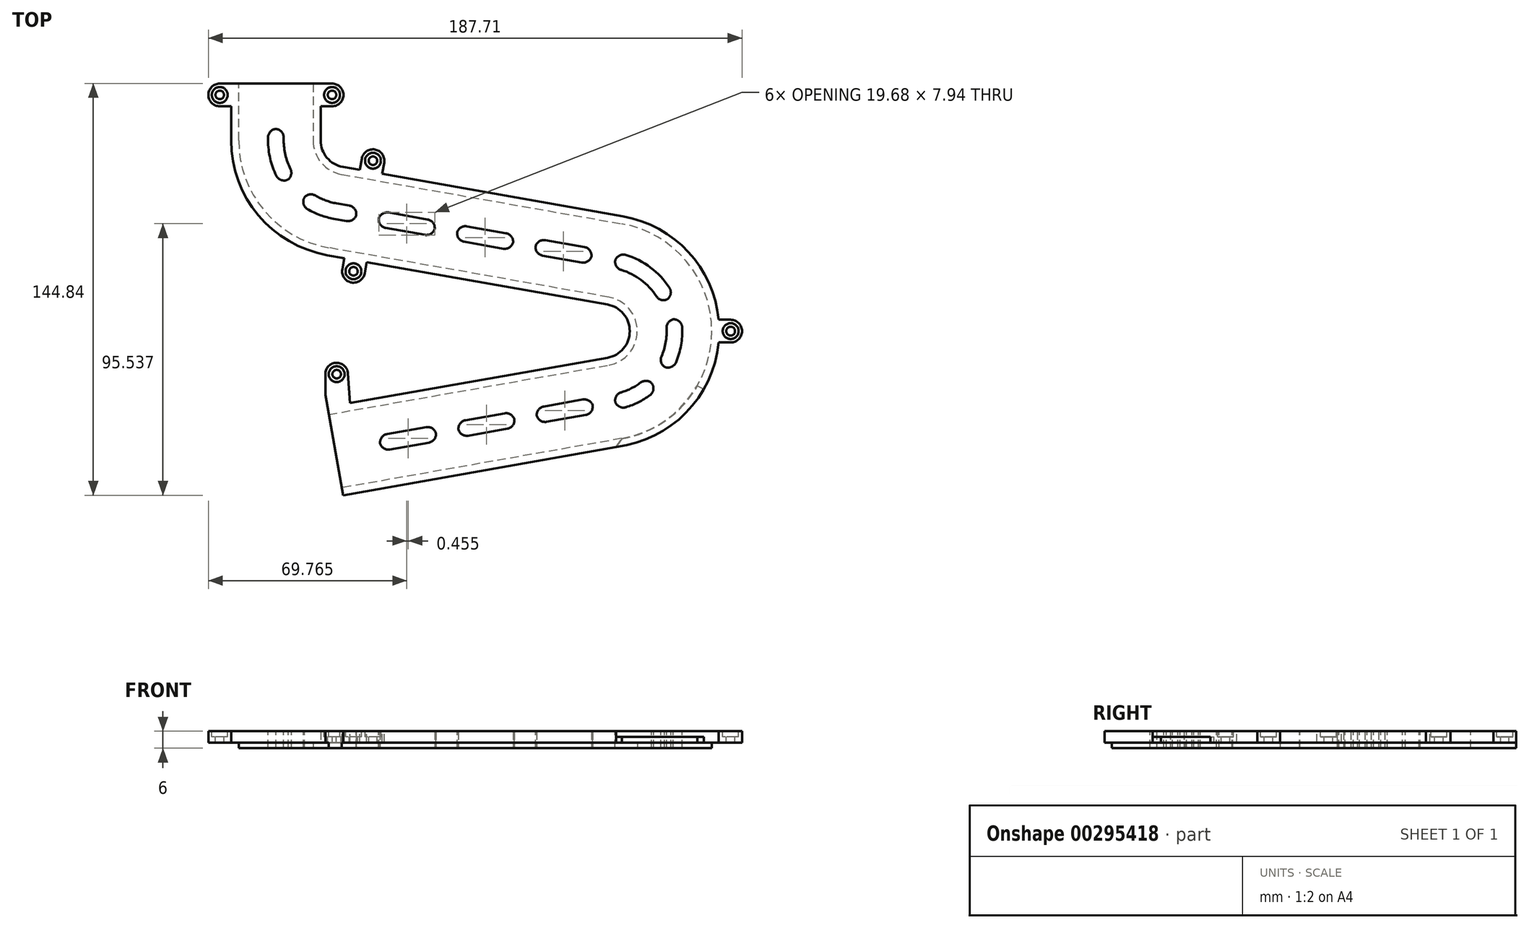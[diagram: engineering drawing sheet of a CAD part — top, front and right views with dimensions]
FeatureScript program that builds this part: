
annotation { "Feature Type Name" : "Feature", "Feature Type Description" : "" }
export const myFeature = defineFeature(function(context is Context, id is Id, definition is map)
    precondition{}
    {
        {
            var Q0;
            Q0=qCreatedBy(makeId("Top.planeOp"),FACE);
            var sketch = newSketch(context, id + "F0", { "sketchPlane" : qUnion([Q0])});
            skArc(sketch, "E0", {"start": v(91.8, -11.82) * mm, "mid": v(101.71, 0) * mm, "end": v(91.8, 11.82) * mm});
            skLineSegment(sketch, "E1", {"start": v(-12, 87.1) * mm, "end": v(-12, 67.1) * mm});
            skArc(sketch, "E2", {"start": v(-12, 67.1) * mm, "mid": v(-9.2, 59.38) * mm, "end": v(-2.08, 55.28) * mm});
            skLineSegment(sketch, "E3", {"start": v(-38.5, 87.1) * mm, "end": v(-38.5, 67.1) * mm});
            skLineSegment(sketch, "E4", {"start": v(-12, 67.1) * mm, "end": v(-38.5, 67.1) * mm, "construction": true});
            skLineSegment(sketch, "E5", {"start": v(91.8, 11.82) * mm, "end": v(-6.69, 29.18) * mm});
            skLineSegment(sketch, "E6", {"start": v(-2.08, 55.28) * mm, "end": v(-6.69, 29.18) * mm, "construction": true});
            skArc(sketch, "E7", {"start": v(96.4, -37.92) * mm, "mid": v(128.21, 0) * mm, "end": v(96.4, 37.92) * mm});
            skLineSegment(sketch, "E8", {"start": v(-2.08, 55.28) * mm, "end": v(96.4, 37.92) * mm});
            skLineSegment(sketch, "E9", {"start": v(96.4, 37.92) * mm, "end": v(91.8, 11.82) * mm, "construction": true});
            skLineSegment(sketch, "E10", {"start": v(91.8, 11.82) * mm, "end": v(91.8, -11.82) * mm, "construction": true});
            skLineSegment(sketch, "E11", {"start": v(91.8, -11.82) * mm, "end": v(-6.69, -29.18) * mm});
            skLineSegment(sketch, "E12", {"start": v(91.8, -11.82) * mm, "end": v(96.4, -37.92) * mm, "construction": true});
            skLineSegment(sketch, "E13", {"start": v(96.4, -37.92) * mm, "end": v(-2.08, -55.28) * mm});
            skLineSegment(sketch, "E14", {"start": v(-6.69, -29.18) * mm, "end": v(-2.08, -55.28) * mm});
            skLineSegment(sketch, "E15", {"start": v(-12, 87.1) * mm, "end": v(-38.5, 87.1) * mm});
            skArc(sketch, "E16.trimOffspring", {"start": v(-38.5, 67.1) * mm, "mid": v(-29.5, 42.35) * mm, "end": v(-6.69, 29.18) * mm});
            skLineSegment(sketch, "E17", {"start": v(0, 67.1) * mm, "end": v(-2.08, 55.28) * mm, "construction": true});
            skLineSegment(sketch, "E18", {"start": v(0, 67.1) * mm, "end": v(-12, 67.1) * mm, "construction": true});
            skSolve(sketch);
        }
        {
            var Q0;
            Q0=qSketchRegion(id+"F0",true);
            extrude(context, id + "F1", {"entities" : qUnion([Q0]), "depth" : 2 * mm});
        }
        {
            var Q0;
            Q0=qCreatedBy(makeId("Top.planeOp"),FACE);
            var sketch = newSketch(context, id + "F2", { "sketchPlane" : qUnion([Q0])});
            skLineSegment(sketch, "E19.0", {"start": v(91.36, -9.36) * mm, "end": v(-7.12, -26.72) * mm});
            skArc(sketch, "E20.0", {"start": v(91.36, -9.36) * mm, "mid": v(99.21, 0) * mm, "end": v(91.36, 9.36) * mm});
            skLineSegment(sketch, "E21.0", {"start": v(91.36, 9.36) * mm, "end": v(-7.12, 26.72) * mm});
            skArc(sketch, "E22.0", {"start": v(-41, 67.1) * mm, "mid": v(-31.4, 40.74) * mm, "end": v(-7.12, 26.72) * mm});
            skLineSegment(sketch, "E23.0", {"start": v(-41, 87.1) * mm, "end": v(-41, 67.1) * mm});
            skLineSegment(sketch, "E24.0", {"start": v(-9.5, 87.1) * mm, "end": v(-9.5, 67.1) * mm});
            skArc(sketch, "E25.0", {"start": v(-9.5, 67.1) * mm, "mid": v(-7.28, 61) * mm, "end": v(-1.65, 57.74) * mm});
            skLineSegment(sketch, "E26.0", {"start": v(-1.65, 57.74) * mm, "end": v(96.83, 40.38) * mm});
            skArc(sketch, "E27.0", {"start": v(96.83, -40.38) * mm, "mid": v(130.71, 0) * mm, "end": v(96.83, 40.38) * mm});
            skLineSegment(sketch, "E28.0", {"start": v(96.83, -40.38) * mm, "end": v(-1.65, -57.74) * mm});
            skLineSegment(sketch, "E29", {"start": v(-12, 87.1) * mm, "end": v(-9.5, 87.1) * mm});
            skLineSegment(sketch, "E30", {"start": v(-38.5, 87.1) * mm, "end": v(-41, 87.1) * mm});
            skLineSegment(sketch, "E31", {"start": v(-6.69, -29.18) * mm, "end": v(-7.12, -26.72) * mm});
            skLineSegment(sketch, "E32", {"start": v(-2.08, -55.28) * mm, "end": v(-1.65, -57.74) * mm});
            skLineSegment(sketch, "E33", {"start": v(-6.69, -29.18) * mm, "end": v(-2.08, -55.28) * mm});
            skLineSegment(sketch, "E34", {"start": v(-38.5, 87.1) * mm, "end": v(-12, 87.1) * mm});
            skLineSegment(sketch, "E35.0", {"start": v(-12, 87.1) * mm, "end": v(-12, 67.1) * mm});
            skLineSegment(sketch, "E36.0", {"start": v(-38.5, 87.1) * mm, "end": v(-38.5, 67.1) * mm});
            skLineSegment(sketch, "E37.0", {"start": v(91.8, -11.82) * mm, "end": v(-6.69, -29.18) * mm});
            skLineSegment(sketch, "E38.0", {"start": v(96.4, -37.92) * mm, "end": v(-2.08, -55.28) * mm});
            skArc(sketch, "E39.0", {"start": v(96.4, -37.92) * mm, "mid": v(128.21, 0) * mm, "end": v(96.4, 37.92) * mm});
            skLineSegment(sketch, "E40.0", {"start": v(-2.08, 55.28) * mm, "end": v(96.4, 37.92) * mm});
            skArc(sketch, "E41.0", {"start": v(-12, 67.1) * mm, "mid": v(-9.2, 59.38) * mm, "end": v(-2.08, 55.28) * mm});
            skArc(sketch, "E42.0", {"start": v(-38.5, 67.1) * mm, "mid": v(-29.5, 42.35) * mm, "end": v(-6.69, 29.18) * mm});
            skLineSegment(sketch, "E43.0", {"start": v(91.8, 11.82) * mm, "end": v(-6.69, 29.18) * mm});
            skArc(sketch, "E44.0", {"start": v(91.8, -11.82) * mm, "mid": v(101.71, 0) * mm, "end": v(91.8, 11.82) * mm});
            skSolve(sketch);
        }
        {
            var Q0;
            Q0 = qSketchRegion(id + "F2", true);
            extrude(context, id + "F3", {"entities" : qUnion([Q0]), "operationType" : NewBodyOperationType.ADD, "depth" : 4 * mm, "hasSecondDirection" : true, "secondDirectionOppositeDirection" : false, "secondDirectionDepth" : 2 * mm});
        }
        {
            var Q0;
            Q0=makeQuery(id+"F3.opExtrude","CAP_FACE",FACE,{"disambiguationData":[OSD([sQuery(id+"F2.wireOp",EDGE,"E19.0"),sQuery(id+"F2.wireOp",EDGE,"E20.0"),sQuery(id+"F2.wireOp",EDGE,"E21.0"),sQuery(id+"F2.wireOp",EDGE,"E22.0"),sQuery(id+"F2.wireOp",EDGE,"E23.0"),sQuery(id+"F2.wireOp",EDGE,"E24.0"),sQuery(id+"F2.wireOp",EDGE,"E25.0"),sQuery(id+"F2.wireOp",EDGE,"E26.0"),sQuery(id+"F2.wireOp",EDGE,"E27.0"),sQuery(id+"F2.wireOp",EDGE,"E28.0"),sQuery(id+"F2.wireOp",EDGE,"E29"),sQuery(id+"F2.wireOp",EDGE,"E30"),sQuery(id+"F2.wireOp",EDGE,"E31"),sQuery(id+"F2.wireOp",EDGE,"E32"),sQuery(id+"F2.wireOp",EDGE,"E33"),sQuery(id+"F2.wireOp",EDGE,"E34")])],"isStart":false});
            extrude(context, id + "F4", {"entities" : qUnion([Q0]), "operationType" : NewBodyOperationType.ADD, "depth" : 2 * mm});
        }
        {
            var Q0;
            Q0=makeQuery(id+"F1.opExtrude","SWEPT_BODY",BODY,{"disambiguationData":[OSD([sQuery(id+"F0.wireOp",EDGE,"E0"),sQuery(id+"F0.wireOp",EDGE,"E1"),sQuery(id+"F0.wireOp",EDGE,"E2"),sQuery(id+"F0.wireOp",EDGE,"E3"),sQuery(id+"F0.wireOp",EDGE,"E5"),sQuery(id+"F0.wireOp",EDGE,"E7"),sQuery(id+"F0.wireOp",EDGE,"E8"),sQuery(id+"F0.wireOp",EDGE,"E11"),sQuery(id+"F0.wireOp",EDGE,"E13"),sQuery(id+"F0.wireOp",EDGE,"E14"),sQuery(id+"F0.wireOp",EDGE,"E15"),sQuery(id+"F0.wireOp",EDGE,"E16.trimOffspring")])]});
            transform(context, id + "F5", {"entities" : qUnion([Q0]), "transformType" : TransformType.TRANSLATION_3D, "dx" : 0 * mm, "dy" : 0 * mm, "dz" : -6 * mm, "makeCopy" : false});
        }
        {
            var Q0;
            Q0=qCreatedBy(makeId("Top.planeOp"),FACE);
            var sketch = newSketch(context, id + "F6", { "sketchPlane" : qUnion([Q0])});
            skLineSegment(sketch, "E45.0", {"start": v(6.23, -56.35) * mm, "end": v(-1.65, -57.74) * mm});
            skLineSegment(sketch, "E46.0", {"start": v(-6.69, -29.18) * mm, "end": v(-2.08, -55.28) * mm, "construction": true});
            skLineSegment(sketch, "E47.0", {"start": v(91.36, -9.36) * mm, "end": v(-7.12, -26.72) * mm, "construction": true});
            skLineSegment(sketch, "E48", {"start": v(-1.65, -57.74) * mm, "end": v(-0.96, -61.68) * mm});
            skLineSegment(sketch, "E49", {"start": v(-4.38, -42.23) * mm, "end": v(8.5, -39.96) * mm, "construction": true});
            skArc(sketch, "E50", {"start": v(-0.96, -61.68) * mm, "mid": v(3.68, -64.93) * mm, "end": v(6.92, -60.3) * mm});
            skLineSegment(sketch, "E51", {"start": v(6.23, -56.35) * mm, "end": v(6.92, -60.3) * mm});
            skPoint(sketch, "E52.orphan", {"position": v(96.83, -40.38) * mm});
            skLineSegment(sketch, "E53.MirrorCS", {"start": v(0.76, -25.33) * mm, "end": v(-7.12, -26.72) * mm});
            skLineSegment(sketch, "E54.MirrorCS", {"start": v(0.76, -25.33) * mm, "end": v(0.06, -21.4) * mm});
            skLineSegment(sketch, "E55.MirrorCS", {"start": v(-7.12, -26.72) * mm, "end": v(-7.81, -22.78) * mm});
            skArc(sketch, "E56.MirrorCS", {"start": v(-7.81, -22.78) * mm, "mid": v(-4.57, -18.15) * mm, "end": v(0.06, -21.4) * mm});
            skSolve(sketch);
        }
        {
            var Q0;
            Q0 = qSketchRegion(id + "F6", true);
            extrude(context, id + "F7", {"entities" : qUnion([Q0]), "operationType" : NewBodyOperationType.ADD, "oppositeDirection" : true, "depth" : 4 * mm});
        }
        {
            var Q0;
            Q0=qCreatedBy(makeId("Top.planeOp"),FACE);
            var sketch = newSketch(context, id + "F8", { "sketchPlane" : qUnion([Q0])});
            skLineSegment(sketch, "E57.0", {"start": v(6.67, 24.29) * mm, "end": v(-1.21, 25.68) * mm});
            skArc(sketch, "E58", {"start": v(-1.9, 21.74) * mm, "mid": v(1.34, 17.1) * mm, "end": v(5.97, 20.35) * mm});
            skLineSegment(sketch, "E59", {"start": v(6.67, 24.29) * mm, "end": v(5.97, 20.35) * mm});
            skLineSegment(sketch, "E60", {"start": v(-1.21, 25.68) * mm, "end": v(-1.9, 21.74) * mm});
            skPoint(sketch, "E61.orphan", {"position": v(91.36, 9.36) * mm});
            skPoint(sketch, "E62.orphan", {"position": v(-7.12, 26.72) * mm});
            skLineSegment(sketch, "E63", {"start": v(-1.65, 57.74) * mm, "end": v(-7.12, 26.72) * mm, "construction": true});
            skLineSegment(sketch, "E64.0", {"start": v(-1.65, 57.74) * mm, "end": v(96.83, 40.38) * mm, "construction": true});
            skLineSegment(sketch, "E65", {"start": v(2.73, 24.98) * mm, "end": v(8.2, 56) * mm, "construction": true});
            skLineSegment(sketch, "E66", {"start": v(5.46, 40.5) * mm, "end": v(34.92, 35.3) * mm, "construction": true});
            skLineSegment(sketch, "E67.MirrorCS", {"start": v(12.14, 55.31) * mm, "end": v(12.83, 59.25) * mm});
            skLineSegment(sketch, "E68.MirrorCS", {"start": v(4.26, 56.7) * mm, "end": v(4.95, 60.64) * mm});
            skLineSegment(sketch, "E69.MirrorCS", {"start": v(12.14, 55.31) * mm, "end": v(4.26, 56.7) * mm});
            skArc(sketch, "E70.MirrorCS", {"start": v(4.95, 60.64) * mm, "mid": v(9.59, 63.88) * mm, "end": v(12.83, 59.25) * mm});
            skSolve(sketch);
        }
        {
            var Q0;
            Q0 = qSketchRegion(id + "F8", true);
            extrude(context, id + "F9", {"entities" : qUnion([Q0]), "operationType" : NewBodyOperationType.ADD, "oppositeDirection" : true, "depth" : 4 * mm});
        }
        {
            var Q0;
            {var subQ0=sQuery(id+"F2.wireOp",EDGE,"E25.0");var subQ1=sQuery(id+"F2.wireOp",EDGE,"E24.0");var subQ2=sQuery(id+"F2.wireOp",EDGE,"E26.0");var subQ3=sQuery(id+"F2.wireOp",EDGE,"E27.0");var subQ4=sQuery(id+"F2.wireOp",EDGE,"E28.0");var subQ5=sQuery(id+"F2.wireOp",EDGE,"E34");var subQ6=sQuery(id+"F2.wireOp",EDGE,"E30");var subQ7=sQuery(id+"F2.wireOp",EDGE,"E29");var subQ8=sQuery(id+"F2.wireOp",EDGE,"E33");var subQ9=sQuery(id+"F2.wireOp",EDGE,"E32");var subQ10=sQuery(id+"F2.wireOp",EDGE,"E31");Q0=makeQuery(id+"F9.boolean.opBoolean","MERGE",FACE,{"derivedFrom":[makeQuery(id+"F7.boolean.opBoolean","MERGE",FACE,{"derivedFrom":[makeQuery(id+"F3.boolean.opBoolean","SPLIT",FACE,{"disambiguationData":[TD([makeQuery(id+"F1.opExtrude","SWEPT_FACE",FACE,{"disambiguationData":[OSD([sQuery(id+"F0.wireOp",EDGE,"E1")])]})])],"derivedFrom":makeQuery(id+"F3.opExtrude","CAP_FACE",FACE,{"disambiguationData":[OSD([sQuery(id+"F2.wireOp",EDGE,"E19.0"),sQuery(id+"F2.wireOp",EDGE,"E20.0"),sQuery(id+"F2.wireOp",EDGE,"E21.0"),sQuery(id+"F2.wireOp",EDGE,"E22.0"),sQuery(id+"F2.wireOp",EDGE,"E23.0"),subQ1,subQ0,subQ2,subQ3,subQ4,subQ7,subQ6,subQ10,subQ9,subQ8,subQ5])],"isStart":true})}),makeQuery(id+"F7.opExtrude","CAP_FACE",FACE,{"disambiguationData":[OSD([sQuery(id+"F6.wireOp",EDGE,"E45.0"),sQuery(id+"F6.wireOp",EDGE,"E48"),sQuery(id+"F6.wireOp",EDGE,"E50"),sQuery(id+"F6.wireOp",EDGE,"E51")])],"isStart":false})]}),makeQuery(id+"F9.opExtrude","CAP_FACE",FACE,{"disambiguationData":[OSD([sQuery(id+"F8.wireOp",EDGE,"aae40222-3721-4959-a5f3-b78c221d8f4e0.MirrorCS"),sQuery(id+"F8.wireOp",EDGE,"aae40222-3721-4959-a5f3-b78c221d8f4e1.MirrorCS"),sQuery(id+"F8.wireOp",EDGE,"aae40222-3721-4959-a5f3-b78c221d8f4e2.MirrorCS"),sQuery(id+"F8.wireOp",EDGE,"aae40222-3721-4959-a5f3-b78c221d8f4e3.MirrorCS")])],"isStart":false})]});}
            var sketch = newSketch(context, id + "F10", { "sketchPlane" : qUnion([Q0])});
            skLineSegment(sketch, "E71.0", {"start": v(-12, -87.1) * mm, "end": v(-38.5, -87.1) * mm, "construction": true});
            skLineSegment(sketch, "E72.0", {"start": v(-9.5, -87.1) * mm, "end": v(-9.5, -83.1) * mm});
            skLineSegment(sketch, "E73.0", {"start": v(-41, -87.1) * mm, "end": v(-41, -67.1) * mm, "construction": true});
            skLineSegment(sketch, "E74", {"start": v(-9.5, -87.1) * mm, "end": v(-5.5, -87.1) * mm});
            skLineSegment(sketch, "E75", {"start": v(-41, -87.1) * mm, "end": v(-58.49, -87.1) * mm, "construction": true});
            skLineSegment(sketch, "E76", {"start": v(-9.5, -79.1) * mm, "end": v(-5.5, -79.1) * mm});
            skArc(sketch, "E77", {"start": v(-5.5, -87.1) * mm, "mid": v(-1.5, -83.1) * mm, "end": v(-5.5, -79.1) * mm});
            skLineSegment(sketch, "E78", {"start": v(-25.25, -87.1) * mm, "end": v(-25.25, -63.64) * mm, "construction": true});
            skPoint(sketch, "E79.orphan", {"position": v(-9.5, -67.1) * mm});
            skLineSegment(sketch, "E80", {"start": v(-9.5, -83.1) * mm, "end": v(-9.5, -79.1) * mm});
            skLineSegment(sketch, "E81.MirrorCS", {"start": v(-38.5, -87.1) * mm, "end": v(-12, -87.1) * mm, "construction": true});
            skLineSegment(sketch, "E82.MirrorCS", {"start": v(-41, -79.1) * mm, "end": v(-45, -79.1) * mm});
            skArc(sketch, "E83.MirrorCS", {"start": v(-45, -87.1) * mm, "mid": v(-49, -83.1) * mm, "end": v(-45, -79.1) * mm});
            skLineSegment(sketch, "E84.MirrorCS", {"start": v(-41, -87.1) * mm, "end": v(-41, -83.1) * mm});
            skLineSegment(sketch, "E85.MirrorCS", {"start": v(-41, -87.1) * mm, "end": v(-45, -87.1) * mm});
            skLineSegment(sketch, "E86.MirrorCS", {"start": v(-41, -83.1) * mm, "end": v(-41, -79.1) * mm});
            skSolve(sketch);
        }
        {
            var Q0;
            Q0 = qSketchRegion(id + "F10", true);
            extrude(context, id + "F11", {"entities" : qUnion([Q0]), "operationType" : NewBodyOperationType.ADD, "oppositeDirection" : true, "depth" : 4 * mm});
        }
        {
            var Q0;
            Q0=makeQuery(id+"F11.boolean.opBoolean","MERGE",FACE,{"derivedFrom":[makeQuery(id+"F9.boolean.opBoolean","MERGE",FACE,{"derivedFrom":[makeQuery(id+"F7.boolean.opBoolean","MERGE",FACE,{"derivedFrom":[makeQuery(id+"F4.opExtrude","CAP_FACE",FACE,{"disambiguationData":[OSD([sQuery(id+"F2.wireOp",EDGE,"E19.0"),sQuery(id+"F2.wireOp",EDGE,"E20.0"),sQuery(id+"F2.wireOp",EDGE,"E21.0"),sQuery(id+"F2.wireOp",EDGE,"E22.0"),sQuery(id+"F2.wireOp",EDGE,"E23.0"),sQuery(id+"F2.wireOp",EDGE,"E24.0"),sQuery(id+"F2.wireOp",EDGE,"E25.0"),sQuery(id+"F2.wireOp",EDGE,"E26.0"),sQuery(id+"F2.wireOp",EDGE,"E27.0"),sQuery(id+"F2.wireOp",EDGE,"E28.0"),sQuery(id+"F2.wireOp",EDGE,"E29"),sQuery(id+"F2.wireOp",EDGE,"E30"),sQuery(id+"F2.wireOp",EDGE,"E31"),sQuery(id+"F2.wireOp",EDGE,"E32"),sQuery(id+"F2.wireOp",EDGE,"E33"),sQuery(id+"F2.wireOp",EDGE,"E34")])],"isStart":false}),makeQuery(id+"F7.opExtrude","CAP_FACE",FACE,{"disambiguationData":[OSD([sQuery(id+"F6.wireOp",EDGE,"E45.0"),sQuery(id+"F6.wireOp",EDGE,"E48"),sQuery(id+"F6.wireOp",EDGE,"E50"),sQuery(id+"F6.wireOp",EDGE,"E51")])],"isStart":true}),makeQuery(id+"F7.opExtrude","CAP_FACE",FACE,{"disambiguationData":[OSD([sQuery(id+"F6.wireOp",EDGE,"E53.MirrorCS"),sQuery(id+"F6.wireOp",EDGE,"E54.MirrorCS"),sQuery(id+"F6.wireOp",EDGE,"E55.MirrorCS"),sQuery(id+"F6.wireOp",EDGE,"E56.MirrorCS")])],"isStart":true})]}),makeQuery(id+"F9.opExtrude","CAP_FACE",FACE,{"disambiguationData":[OSD([sQuery(id+"F8.wireOp",EDGE,"E57.0"),sQuery(id+"F8.wireOp",EDGE,"E58"),sQuery(id+"F8.wireOp",EDGE,"E59"),sQuery(id+"F8.wireOp",EDGE,"E60")])],"isStart":true}),makeQuery(id+"F9.opExtrude","CAP_FACE",FACE,{"disambiguationData":[OSD([sQuery(id+"F8.wireOp",EDGE,"aae40222-3721-4959-a5f3-b78c221d8f4e0.MirrorCS"),sQuery(id+"F8.wireOp",EDGE,"aae40222-3721-4959-a5f3-b78c221d8f4e1.MirrorCS"),sQuery(id+"F8.wireOp",EDGE,"aae40222-3721-4959-a5f3-b78c221d8f4e2.MirrorCS"),sQuery(id+"F8.wireOp",EDGE,"aae40222-3721-4959-a5f3-b78c221d8f4e3.MirrorCS")])],"isStart":true})]}),makeQuery(id+"F11.opExtrude","CAP_FACE",FACE,{"disambiguationData":[OSD([sQuery(id+"F10.wireOp",EDGE,"E72.0"),sQuery(id+"F10.wireOp",EDGE,"E74"),sQuery(id+"F10.wireOp",EDGE,"E76"),sQuery(id+"F10.wireOp",EDGE,"E77"),sQuery(id+"F10.wireOp",EDGE,"E80")])],"isStart":false}),makeQuery(id+"F11.opExtrude","CAP_FACE",FACE,{"disambiguationData":[OSD([sQuery(id+"F10.wireOp",EDGE,"E82.MirrorCS"),sQuery(id+"F10.wireOp",EDGE,"E83.MirrorCS"),sQuery(id+"F10.wireOp",EDGE,"E84.MirrorCS"),sQuery(id+"F10.wireOp",EDGE,"E85.MirrorCS"),sQuery(id+"F10.wireOp",EDGE,"E86.MirrorCS")])],"isStart":false})]});
            var sketch = newSketch(context, id + "F12", { "sketchPlane" : qUnion([Q0])});
            skArc(sketch, "E87.0", {"start": v(-5.5, 87.1) * mm, "mid": v(-1.5, 83.1) * mm, "end": v(-5.5, 79.1) * mm, "construction": true});
            skArc(sketch, "E88.0", {"start": v(-1.9, 21.74) * mm, "mid": v(1.34, 17.1) * mm, "end": v(5.97, 20.35) * mm, "construction": true});
            skArc(sketch, "E89.0", {"start": v(-7.81, -22.78) * mm, "mid": v(-4.57, -18.15) * mm, "end": v(0.06, -21.4) * mm, "construction": true});
            skArc(sketch, "E90.0", {"start": v(-0.96, -61.68) * mm, "mid": v(3.68, -64.93) * mm, "end": v(6.92, -60.3) * mm, "construction": true});
            skArc(sketch, "E91.0", {"start": v(-45, 87.1) * mm, "mid": v(-49, 83.1) * mm, "end": v(-45, 79.1) * mm, "construction": true});
            skCircle(sketch, "E92", {"center": v(-45, 83.1) * mm, "radius": 2.8 * mm});
            skCircle(sketch, "E93", {"center": v(-5.5, 83.1) * mm, "radius": 2.8 * mm});
            skCircle(sketch, "E94", {"center": v(2.03, 21.04) * mm, "radius": 2.8 * mm});
            skCircle(sketch, "E95", {"center": v(-3.87, -22.09) * mm, "radius": 2.8 * mm});
            skCircle(sketch, "E96", {"center": v(2.98, -60.99) * mm, "radius": 2.8 * mm});
            skLineSegment(sketch, "E97", {"start": v(-1.65, 57.74) * mm, "end": v(-7.12, 26.72) * mm, "construction": true});
            skLineSegment(sketch, "E98", {"start": v(-4.38, 42.23) * mm, "end": v(23.58, 37.3) * mm, "construction": true});
            skCircle(sketch, "E99.MirrorC", {"center": v(8.9, 59.94) * mm, "radius": 2.8 * mm});
            skArc(sketch, "E100.MirrorCS", {"start": v(4.95, 60.64) * mm, "mid": v(9.59, 63.88) * mm, "end": v(12.83, 59.25) * mm, "construction": true});
            skSolve(sketch);
        }
        {
            var Q0;
            Q0 = qSketchRegion(id + "F12", true);
            extrude(context, id + "F13", {"entities" : qUnion([Q0]), "operationType" : NewBodyOperationType.REMOVE, "oppositeDirection" : true, "depth" : 2 * mm});
        }
        {
            var Q0;
            Q0=makeQuery(id+"F11.boolean.opBoolean","MERGE",FACE,{"derivedFrom":[makeQuery(id+"F9.boolean.opBoolean","MERGE",FACE,{"derivedFrom":[makeQuery(id+"F7.boolean.opBoolean","MERGE",FACE,{"derivedFrom":[makeQuery(id+"F4.opExtrude","CAP_FACE",FACE,{"disambiguationData":[OSD([sQuery(id+"F2.wireOp",EDGE,"E19.0"),sQuery(id+"F2.wireOp",EDGE,"E20.0"),sQuery(id+"F2.wireOp",EDGE,"E21.0"),sQuery(id+"F2.wireOp",EDGE,"E22.0"),sQuery(id+"F2.wireOp",EDGE,"E23.0"),sQuery(id+"F2.wireOp",EDGE,"E24.0"),sQuery(id+"F2.wireOp",EDGE,"E25.0"),sQuery(id+"F2.wireOp",EDGE,"E26.0"),sQuery(id+"F2.wireOp",EDGE,"E27.0"),sQuery(id+"F2.wireOp",EDGE,"E28.0"),sQuery(id+"F2.wireOp",EDGE,"E29"),sQuery(id+"F2.wireOp",EDGE,"E30"),sQuery(id+"F2.wireOp",EDGE,"E31"),sQuery(id+"F2.wireOp",EDGE,"E32"),sQuery(id+"F2.wireOp",EDGE,"E33"),sQuery(id+"F2.wireOp",EDGE,"E34")])],"isStart":false}),makeQuery(id+"F7.opExtrude","CAP_FACE",FACE,{"disambiguationData":[OSD([sQuery(id+"F6.wireOp",EDGE,"E45.0"),sQuery(id+"F6.wireOp",EDGE,"E48"),sQuery(id+"F6.wireOp",EDGE,"E50"),sQuery(id+"F6.wireOp",EDGE,"E51")])],"isStart":true}),makeQuery(id+"F7.opExtrude","CAP_FACE",FACE,{"disambiguationData":[OSD([sQuery(id+"F6.wireOp",EDGE,"E53.MirrorCS"),sQuery(id+"F6.wireOp",EDGE,"E54.MirrorCS"),sQuery(id+"F6.wireOp",EDGE,"E55.MirrorCS"),sQuery(id+"F6.wireOp",EDGE,"E56.MirrorCS")])],"isStart":true})]}),makeQuery(id+"F9.opExtrude","CAP_FACE",FACE,{"disambiguationData":[OSD([sQuery(id+"F8.wireOp",EDGE,"E57.0"),sQuery(id+"F8.wireOp",EDGE,"E58"),sQuery(id+"F8.wireOp",EDGE,"E59"),sQuery(id+"F8.wireOp",EDGE,"E60")])],"isStart":true}),makeQuery(id+"F9.opExtrude","CAP_FACE",FACE,{"disambiguationData":[OSD([sQuery(id+"F8.wireOp",EDGE,"aae40222-3721-4959-a5f3-b78c221d8f4e0.MirrorCS"),sQuery(id+"F8.wireOp",EDGE,"aae40222-3721-4959-a5f3-b78c221d8f4e1.MirrorCS"),sQuery(id+"F8.wireOp",EDGE,"aae40222-3721-4959-a5f3-b78c221d8f4e2.MirrorCS"),sQuery(id+"F8.wireOp",EDGE,"aae40222-3721-4959-a5f3-b78c221d8f4e3.MirrorCS")])],"isStart":true})]}),makeQuery(id+"F11.opExtrude","CAP_FACE",FACE,{"disambiguationData":[OSD([sQuery(id+"F10.wireOp",EDGE,"E72.0"),sQuery(id+"F10.wireOp",EDGE,"E74"),sQuery(id+"F10.wireOp",EDGE,"E76"),sQuery(id+"F10.wireOp",EDGE,"E77"),sQuery(id+"F10.wireOp",EDGE,"E80")])],"isStart":false}),makeQuery(id+"F11.opExtrude","CAP_FACE",FACE,{"disambiguationData":[OSD([sQuery(id+"F10.wireOp",EDGE,"E82.MirrorCS"),sQuery(id+"F10.wireOp",EDGE,"E83.MirrorCS"),sQuery(id+"F10.wireOp",EDGE,"E84.MirrorCS"),sQuery(id+"F10.wireOp",EDGE,"E85.MirrorCS"),sQuery(id+"F10.wireOp",EDGE,"E86.MirrorCS")])],"isStart":false})]});
            var sketch = newSketch(context, id + "F14", { "sketchPlane" : qUnion([Q0])});
            skCircle(sketch, "E101.0.0", {"center": v(-5.5, 83.1) * mm, "radius": 2.8 * mm, "construction": true});
            skCircle(sketch, "E102.0", {"center": v(-45, 83.1) * mm, "radius": 2.8 * mm, "construction": true});
            skCircle(sketch, "E103.0", {"center": v(8.9, 59.94) * mm, "radius": 2.8 * mm, "construction": true});
            skCircle(sketch, "E104.0.0", {"center": v(2.03, 21.04) * mm, "radius": 2.8 * mm, "construction": true});
            skCircle(sketch, "E105.0", {"center": v(-3.87, -22.09) * mm, "radius": 2.8 * mm, "construction": true});
            skCircle(sketch, "E106.0", {"center": v(2.98, -60.99) * mm, "radius": 2.8 * mm, "construction": true});
            skCircle(sketch, "E107", {"center": v(2.98, -60.99) * mm, "radius": 1.5 * mm});
            skCircle(sketch, "E108", {"center": v(-3.87, -22.09) * mm, "radius": 1.5 * mm});
            skCircle(sketch, "E109", {"center": v(2.03, 21.04) * mm, "radius": 1.5 * mm});
            skCircle(sketch, "E110", {"center": v(8.9, 59.94) * mm, "radius": 1.5 * mm});
            skCircle(sketch, "E111", {"center": v(-5.5, 83.1) * mm, "radius": 1.5 * mm});
            skCircle(sketch, "E112", {"center": v(-45, 83.1) * mm, "radius": 1.5 * mm});
            skSolve(sketch);
        }
        {
            var Q0;
            Q0 = qSketchRegion(id + "F14", true);
            extrude(context, id + "F15", {"entities" : qUnion([Q0]), "operationType" : NewBodyOperationType.REMOVE, "oppositeDirection" : true, "depth" : 25 * mm});
        }
        {
            var Q0;
            Q0=makeQuery(id+"F11.boolean.opBoolean","MERGE",FACE,{"derivedFrom":[makeQuery(id+"F9.boolean.opBoolean","MERGE",FACE,{"derivedFrom":[makeQuery(id+"F7.boolean.opBoolean","MERGE",FACE,{"derivedFrom":[makeQuery(id+"F4.opExtrude","CAP_FACE",FACE,{"disambiguationData":[OSD([sQuery(id+"F2.wireOp",EDGE,"E19.0"),sQuery(id+"F2.wireOp",EDGE,"E20.0"),sQuery(id+"F2.wireOp",EDGE,"E21.0"),sQuery(id+"F2.wireOp",EDGE,"E22.0"),sQuery(id+"F2.wireOp",EDGE,"E23.0"),sQuery(id+"F2.wireOp",EDGE,"E24.0"),sQuery(id+"F2.wireOp",EDGE,"E25.0"),sQuery(id+"F2.wireOp",EDGE,"E26.0"),sQuery(id+"F2.wireOp",EDGE,"E27.0"),sQuery(id+"F2.wireOp",EDGE,"E28.0"),sQuery(id+"F2.wireOp",EDGE,"E29"),sQuery(id+"F2.wireOp",EDGE,"E30"),sQuery(id+"F2.wireOp",EDGE,"E31"),sQuery(id+"F2.wireOp",EDGE,"E32"),sQuery(id+"F2.wireOp",EDGE,"E33"),sQuery(id+"F2.wireOp",EDGE,"E34")])],"isStart":false}),makeQuery(id+"F7.opExtrude","CAP_FACE",FACE,{"disambiguationData":[OSD([sQuery(id+"F6.wireOp",EDGE,"E45.0"),sQuery(id+"F6.wireOp",EDGE,"E48"),sQuery(id+"F6.wireOp",EDGE,"E50"),sQuery(id+"F6.wireOp",EDGE,"E51")])],"isStart":true}),makeQuery(id+"F7.opExtrude","CAP_FACE",FACE,{"disambiguationData":[OSD([sQuery(id+"F6.wireOp",EDGE,"E53.MirrorCS"),sQuery(id+"F6.wireOp",EDGE,"E54.MirrorCS"),sQuery(id+"F6.wireOp",EDGE,"E55.MirrorCS"),sQuery(id+"F6.wireOp",EDGE,"E56.MirrorCS")])],"isStart":true})]}),makeQuery(id+"F9.opExtrude","CAP_FACE",FACE,{"disambiguationData":[OSD([sQuery(id+"F8.wireOp",EDGE,"E57.0"),sQuery(id+"F8.wireOp",EDGE,"E58"),sQuery(id+"F8.wireOp",EDGE,"E59"),sQuery(id+"F8.wireOp",EDGE,"E60")])],"isStart":true}),makeQuery(id+"F9.opExtrude","CAP_FACE",FACE,{"disambiguationData":[OSD([sQuery(id+"F8.wireOp",EDGE,"E67.MirrorCS"),sQuery(id+"F8.wireOp",EDGE,"E68.MirrorCS"),sQuery(id+"F8.wireOp",EDGE,"E69.MirrorCS"),sQuery(id+"F8.wireOp",EDGE,"E70.MirrorCS")])],"isStart":true})]}),makeQuery(id+"F11.opExtrude","CAP_FACE",FACE,{"disambiguationData":[OSD([sQuery(id+"F10.wireOp",EDGE,"E72.0"),sQuery(id+"F10.wireOp",EDGE,"E74"),sQuery(id+"F10.wireOp",EDGE,"E76"),sQuery(id+"F10.wireOp",EDGE,"E77"),sQuery(id+"F10.wireOp",EDGE,"E80")])],"isStart":false}),makeQuery(id+"F11.opExtrude","CAP_FACE",FACE,{"disambiguationData":[OSD([sQuery(id+"F10.wireOp",EDGE,"E82.MirrorCS"),sQuery(id+"F10.wireOp",EDGE,"E83.MirrorCS"),sQuery(id+"F10.wireOp",EDGE,"E84.MirrorCS"),sQuery(id+"F10.wireOp",EDGE,"E85.MirrorCS"),sQuery(id+"F10.wireOp",EDGE,"E86.MirrorCS")])],"isStart":false})]});
            var sketch = newSketch(context, id + "F16", { "sketchPlane" : qUnion([Q0])});
            skArc(sketch, "E113.0", {"start": v(96.83, -40.38) * mm, "mid": v(113.23, -33.59) * mm, "end": v(125.22, -20.5) * mm});
            skLineSegment(sketch, "E114", {"start": v(96.83, -40.38) * mm, "end": v(96.4, -37.92) * mm});
            skLineSegment(sketch, "E115", {"start": v(123.05, -19.25) * mm, "end": v(125.22, -20.5) * mm});
            skArc(sketch, "E116.0", {"start": v(96.4, -37.92) * mm, "mid": v(111.8, -31.54) * mm, "end": v(123.05, -19.25) * mm});
            skPoint(sketch, "E117.orphan", {"position": v(96.4, 37.92) * mm});
            skPoint(sketch, "E118.orphan", {"position": v(96.83, 40.38) * mm});
            skSolve(sketch);
        }
        {
            var Q0;
            Q0 = qSketchRegion(id + "F16", true);
            extrude(context, id + "F17", {"entities" : qUnion([Q0]), "operationType" : NewBodyOperationType.REMOVE, "oppositeDirection" : true, "depth" : 25 * mm});
        }
        {
            var Q0;
            Q0=makeQuery(id+"F17.boolean.opBoolean","COPY",EDGE,{"derivedFrom":makeQuery(id+"F17.opExtrude","SWEPT_EDGE",EDGE,{"disambiguationData":[OSD([sQuery(id+"F2.wireOp",EDGE,"E27.0"),sQuery(id+"F16.wireOp",EDGE,"E113.0"),sQuery(id+"F16.wireOp",EDGE,"E115")])]})});
            var Q1;
            {var subQ0=sQuery(id+"F2.wireOp",EDGE,"E28.0");var subQ1=sQuery(id+"F2.wireOp",EDGE,"E27.0");Q1=makeQuery(id+"F17.boolean.opBoolean","MERGE",EDGE,{"derivedFrom":[makeQuery(id+"F4.boolean.opBoolean","MERGE",EDGE,{"derivedFrom":[makeQuery(id+"F3.opExtrude","SWEPT_EDGE",EDGE,{"disambiguationData":[OSD([subQ1,subQ0])]}),makeQuery(id+"F4.opExtrude","SWEPT_EDGE",EDGE,{"disambiguationData":[OSD([subQ1,subQ0])]})]}),makeQuery(id+"F17.opExtrude","SWEPT_EDGE",EDGE,{"disambiguationData":[OSD([subQ0,sQuery(id+"F16.wireOp",EDGE,"E113.0"),sQuery(id+"F16.wireOp",EDGE,"E114")])]})]});}
            chamfer(context, id + "F18", {"entities" : qUnion([Q0, Q1]), "width" : 2.5 * mm, "tangentPropagation" : true});
        }
        {
            var Q0;
            Q0=makeQuery(id+"F11.boolean.opBoolean","MERGE",FACE,{"derivedFrom":[makeQuery(id+"F9.boolean.opBoolean","MERGE",FACE,{"derivedFrom":[makeQuery(id+"F7.boolean.opBoolean","MERGE",FACE,{"derivedFrom":[makeQuery(id+"F4.opExtrude","CAP_FACE",FACE,{"disambiguationData":[OSD([sQuery(id+"F2.wireOp",EDGE,"E19.0"),sQuery(id+"F2.wireOp",EDGE,"E20.0"),sQuery(id+"F2.wireOp",EDGE,"E21.0"),sQuery(id+"F2.wireOp",EDGE,"E22.0"),sQuery(id+"F2.wireOp",EDGE,"E23.0"),sQuery(id+"F2.wireOp",EDGE,"E24.0"),sQuery(id+"F2.wireOp",EDGE,"E25.0"),sQuery(id+"F2.wireOp",EDGE,"E26.0"),sQuery(id+"F2.wireOp",EDGE,"E27.0"),sQuery(id+"F2.wireOp",EDGE,"E28.0"),sQuery(id+"F2.wireOp",EDGE,"E29"),sQuery(id+"F2.wireOp",EDGE,"E30"),sQuery(id+"F2.wireOp",EDGE,"E31"),sQuery(id+"F2.wireOp",EDGE,"E32"),sQuery(id+"F2.wireOp",EDGE,"E33"),sQuery(id+"F2.wireOp",EDGE,"E34")])],"isStart":false}),makeQuery(id+"F7.opExtrude","CAP_FACE",FACE,{"disambiguationData":[OSD([sQuery(id+"F6.wireOp",EDGE,"E45.0"),sQuery(id+"F6.wireOp",EDGE,"E48"),sQuery(id+"F6.wireOp",EDGE,"E50"),sQuery(id+"F6.wireOp",EDGE,"E51")])],"isStart":true}),makeQuery(id+"F7.opExtrude","CAP_FACE",FACE,{"disambiguationData":[OSD([sQuery(id+"F6.wireOp",EDGE,"E53.MirrorCS"),sQuery(id+"F6.wireOp",EDGE,"E54.MirrorCS"),sQuery(id+"F6.wireOp",EDGE,"E55.MirrorCS"),sQuery(id+"F6.wireOp",EDGE,"E56.MirrorCS")])],"isStart":true})]}),makeQuery(id+"F9.opExtrude","CAP_FACE",FACE,{"disambiguationData":[OSD([sQuery(id+"F8.wireOp",EDGE,"E57.0"),sQuery(id+"F8.wireOp",EDGE,"E58"),sQuery(id+"F8.wireOp",EDGE,"E59"),sQuery(id+"F8.wireOp",EDGE,"E60")])],"isStart":true}),makeQuery(id+"F9.opExtrude","CAP_FACE",FACE,{"disambiguationData":[OSD([sQuery(id+"F8.wireOp",EDGE,"E67.MirrorCS"),sQuery(id+"F8.wireOp",EDGE,"E68.MirrorCS"),sQuery(id+"F8.wireOp",EDGE,"E69.MirrorCS"),sQuery(id+"F8.wireOp",EDGE,"E70.MirrorCS")])],"isStart":true})]}),makeQuery(id+"F11.opExtrude","CAP_FACE",FACE,{"disambiguationData":[OSD([sQuery(id+"F10.wireOp",EDGE,"E72.0"),sQuery(id+"F10.wireOp",EDGE,"E74"),sQuery(id+"F10.wireOp",EDGE,"E76"),sQuery(id+"F10.wireOp",EDGE,"E77"),sQuery(id+"F10.wireOp",EDGE,"E80")])],"isStart":false}),makeQuery(id+"F11.opExtrude","CAP_FACE",FACE,{"disambiguationData":[OSD([sQuery(id+"F10.wireOp",EDGE,"E82.MirrorCS"),sQuery(id+"F10.wireOp",EDGE,"E83.MirrorCS"),sQuery(id+"F10.wireOp",EDGE,"E84.MirrorCS"),sQuery(id+"F10.wireOp",EDGE,"E85.MirrorCS"),sQuery(id+"F10.wireOp",EDGE,"E86.MirrorCS")])],"isStart":false})]});
            var sketch = newSketch(context, id + "F19", { "sketchPlane" : qUnion([Q0])});
            skArc(sketch, "E119.0", {"start": v(96.4, -37.92) * mm, "mid": v(111.83, -31.51) * mm, "end": v(123.1, -19.17) * mm});
            skLineSegment(sketch, "E120.0", {"start": v(123.1, -19.17) * mm, "end": v(126.47, -18.15) * mm});
            skLineSegment(sketch, "E121.0", {"start": v(94.37, -40.81) * mm, "end": v(96.4, -37.92) * mm});
            skArc(sketch, "E122", {"start": v(94.43, -40.73) * mm, "mid": v(113.32, -33.52) * mm, "end": v(126.47, -18.15) * mm});
            skSolve(sketch);
        }
        {
            var Q0;
            Q0 = qSketchRegion(id + "F19", true);
            extrude(context, id + "F20", {"entities" : qUnion([Q0]), "operationType" : NewBodyOperationType.ADD, "oppositeDirection" : true, "depth" : 2 * mm});
        }
        {
            var Q0;
            Q0=makeQuery(id+"F1.opExtrude","CAP_FACE",FACE,{"disambiguationData":[OSD([sQuery(id+"F0.wireOp",EDGE,"E0"),sQuery(id+"F0.wireOp",EDGE,"E1"),sQuery(id+"F0.wireOp",EDGE,"E2"),sQuery(id+"F0.wireOp",EDGE,"E3"),sQuery(id+"F0.wireOp",EDGE,"E5"),sQuery(id+"F0.wireOp",EDGE,"E7"),sQuery(id+"F0.wireOp",EDGE,"E8"),sQuery(id+"F0.wireOp",EDGE,"E11"),sQuery(id+"F0.wireOp",EDGE,"E13"),sQuery(id+"F0.wireOp",EDGE,"E14"),sQuery(id+"F0.wireOp",EDGE,"E15"),sQuery(id+"F0.wireOp",EDGE,"E16.trimOffspring")])],"isStart":true});
            var sketch = newSketch(context, id + "F21", { "sketchPlane" : qUnion([Q0])});
            skLineSegment(sketch, "E123.0.0", {"start": v(-2.08, -55.28) * mm, "end": v(96.4, -37.92) * mm});
            skArc(sketch, "E123.0.1", {"start": v(96.4, -37.92) * mm, "mid": v(128.21, 0) * mm, "end": v(96.4, 37.92) * mm});
            skLineSegment(sketch, "E123.0.2", {"start": v(96.4, 37.92) * mm, "end": v(-2.08, 55.28) * mm});
            skLineSegment(sketch, "E123.0.3", {"start": v(-2.08, 55.28) * mm, "end": v(-2.1, 55.13) * mm});
            skLineSegment(sketch, "E123.0.4", {"start": v(-6.69, 29.18) * mm, "end": v(91.8, 11.82) * mm});
            skArc(sketch, "E123.0.5", {"start": v(91.8, 11.82) * mm, "mid": v(101.71, 0) * mm, "end": v(91.8, -11.82) * mm});
            skLineSegment(sketch, "E123.0.6", {"start": v(91.8, -11.82) * mm, "end": v(-6.69, -29.18) * mm});
            skArc(sketch, "E123.0.7", {"start": v(-6.69, -29.18) * mm, "mid": v(-29.5, -42.35) * mm, "end": v(-38.5, -67.1) * mm});
            skLineSegment(sketch, "E123.0.8", {"start": v(-38.5, -67.1) * mm, "end": v(-38.5, -87.1) * mm});
            skLineSegment(sketch, "E123.0.9", {"start": v(-38.5, -87.1) * mm, "end": v(-38.35, -87.1) * mm});
            skLineSegment(sketch, "E123.0.10", {"start": v(-12, -87.1) * mm, "end": v(-12, -67.1) * mm});
            skArc(sketch, "E123.0.11", {"start": v(-12, -67.1) * mm, "mid": v(-9.2, -59.38) * mm, "end": v(-2.08, -55.28) * mm});
            skArc(sketch, "E124.0", {"start": v(-12.15, -67.1) * mm, "mid": v(-9.3, -59.29) * mm, "end": v(-2.1, -55.13) * mm});
            skLineSegment(sketch, "E124.1", {"start": v(-6.66, 29.33) * mm, "end": v(91.82, 11.97) * mm});
            skLineSegment(sketch, "E124.3", {"start": v(96.37, 37.77) * mm, "end": v(-2.1, 55.13) * mm});
            skArc(sketch, "E124.4", {"start": v(96.37, -37.77) * mm, "mid": v(128.06, 0) * mm, "end": v(96.37, 37.77) * mm});
            skArc(sketch, "E124.5", {"start": v(91.82, 11.97) * mm, "mid": v(101.86, 0) * mm, "end": v(91.82, -11.97) * mm});
            skLineSegment(sketch, "E124.6", {"start": v(-2.1, -55.13) * mm, "end": v(96.37, -37.77) * mm});
            skLineSegment(sketch, "E124.7", {"start": v(91.82, -11.97) * mm, "end": v(-6.66, -29.33) * mm});
            skArc(sketch, "E124.8", {"start": v(-6.66, -29.33) * mm, "mid": v(-29.38, -42.45) * mm, "end": v(-38.35, -67.1) * mm});
            skLineSegment(sketch, "E124.9", {"start": v(-38.35, -67.1) * mm, "end": v(-38.35, -87.1) * mm});
            skLineSegment(sketch, "E124.11", {"start": v(-12.15, -87.1) * mm, "end": v(-12.15, -67.1) * mm});
            skLineSegment(sketch, "E125.trimOffspring", {"start": v(-12.15, -87.1) * mm, "end": v(-12, -87.1) * mm});
            skLineSegment(sketch, "E126.trimOffspring", {"start": v(-6.66, 29.33) * mm, "end": v(-6.69, 29.18) * mm});
            skSolve(sketch);
        }
        {
            var Q0;
            Q0 = qSketchRegion(id + "F21", true);
            var Q1;
            {var subQ0=sQuery(id+"F2.wireOp",EDGE,"E20.0");var subQ1=sQuery(id+"F2.wireOp",EDGE,"E19.0");var subQ2=sQuery(id+"F2.wireOp",EDGE,"E21.0");var subQ3=sQuery(id+"F2.wireOp",EDGE,"E22.0");var subQ4=sQuery(id+"F2.wireOp",EDGE,"E23.0");var subQ5=sQuery(id+"F2.wireOp",EDGE,"E34");var subQ6=sQuery(id+"F2.wireOp",EDGE,"E30");var subQ7=sQuery(id+"F2.wireOp",EDGE,"E29");var subQ8=sQuery(id+"F2.wireOp",EDGE,"E33");var subQ9=sQuery(id+"F2.wireOp",EDGE,"E32");var subQ10=sQuery(id+"F2.wireOp",EDGE,"E31");Q1=makeQuery(id+"F11.boolean.opBoolean","MERGE",FACE,{"derivedFrom":[makeQuery(id+"F9.boolean.opBoolean","MERGE",FACE,{"derivedFrom":[makeQuery(id+"F7.boolean.opBoolean","MERGE",FACE,{"derivedFrom":[makeQuery(id+"F3.boolean.opBoolean","SPLIT",FACE,{"disambiguationData":[TD([makeQuery(id+"F1.opExtrude","SWEPT_FACE",FACE,{"disambiguationData":[OSD([sQuery(id+"F0.wireOp",EDGE,"E0")])]})])],"derivedFrom":makeQuery(id+"F3.opExtrude","CAP_FACE",FACE,{"disambiguationData":[OSD([subQ1,subQ0,subQ2,subQ3,subQ4,sQuery(id+"F2.wireOp",EDGE,"E24.0"),sQuery(id+"F2.wireOp",EDGE,"E25.0"),sQuery(id+"F2.wireOp",EDGE,"E26.0"),sQuery(id+"F2.wireOp",EDGE,"E27.0"),sQuery(id+"F2.wireOp",EDGE,"E28.0"),subQ7,subQ6,subQ10,subQ9,subQ8,subQ5])],"isStart":true})}),makeQuery(id+"F7.opExtrude","CAP_FACE",FACE,{"disambiguationData":[OSD([sQuery(id+"F6.wireOp",EDGE,"E53.MirrorCS"),sQuery(id+"F6.wireOp",EDGE,"E54.MirrorCS"),sQuery(id+"F6.wireOp",EDGE,"E55.MirrorCS"),sQuery(id+"F6.wireOp",EDGE,"E56.MirrorCS")])],"isStart":false})]}),makeQuery(id+"F9.opExtrude","CAP_FACE",FACE,{"disambiguationData":[OSD([sQuery(id+"F8.wireOp",EDGE,"E57.0"),sQuery(id+"F8.wireOp",EDGE,"E58"),sQuery(id+"F8.wireOp",EDGE,"E59"),sQuery(id+"F8.wireOp",EDGE,"E60")])],"isStart":false})]}),makeQuery(id+"F11.opExtrude","CAP_FACE",FACE,{"disambiguationData":[OSD([sQuery(id+"F10.wireOp",EDGE,"E82.MirrorCS"),sQuery(id+"F10.wireOp",EDGE,"E83.MirrorCS"),sQuery(id+"F10.wireOp",EDGE,"E84.MirrorCS"),sQuery(id+"F10.wireOp",EDGE,"E85.MirrorCS"),sQuery(id+"F10.wireOp",EDGE,"E86.MirrorCS")])],"isStart":true})]});}
            extrude(context, id + "F22", {"entities" : qUnion([Q0]), "operationType" : NewBodyOperationType.REMOVE, "endBound" : BoundingType.UP_TO_SURFACE, "oppositeDirection" : true, "endBoundEntityFace" : qUnion([Q1]), "depth" : 25 * mm});
        }
        {
            var Q0;
            Q0=makeQuery(id+"F20.boolean.opBoolean","MERGE",FACE,{"derivedFrom":[makeQuery(id+"F11.boolean.opBoolean","MERGE",FACE,{"derivedFrom":[makeQuery(id+"F9.boolean.opBoolean","MERGE",FACE,{"derivedFrom":[makeQuery(id+"F7.boolean.opBoolean","MERGE",FACE,{"derivedFrom":[makeQuery(id+"F4.opExtrude","CAP_FACE",FACE,{"disambiguationData":[OSD([sQuery(id+"F2.wireOp",EDGE,"E19.0"),sQuery(id+"F2.wireOp",EDGE,"E20.0"),sQuery(id+"F2.wireOp",EDGE,"E21.0"),sQuery(id+"F2.wireOp",EDGE,"E22.0"),sQuery(id+"F2.wireOp",EDGE,"E23.0"),sQuery(id+"F2.wireOp",EDGE,"E24.0"),sQuery(id+"F2.wireOp",EDGE,"E25.0"),sQuery(id+"F2.wireOp",EDGE,"E26.0"),sQuery(id+"F2.wireOp",EDGE,"E27.0"),sQuery(id+"F2.wireOp",EDGE,"E28.0"),sQuery(id+"F2.wireOp",EDGE,"E29"),sQuery(id+"F2.wireOp",EDGE,"E30"),sQuery(id+"F2.wireOp",EDGE,"E31"),sQuery(id+"F2.wireOp",EDGE,"E32"),sQuery(id+"F2.wireOp",EDGE,"E33"),sQuery(id+"F2.wireOp",EDGE,"E34")])],"isStart":false}),makeQuery(id+"F7.opExtrude","CAP_FACE",FACE,{"disambiguationData":[OSD([sQuery(id+"F6.wireOp",EDGE,"E45.0"),sQuery(id+"F6.wireOp",EDGE,"E48"),sQuery(id+"F6.wireOp",EDGE,"E50"),sQuery(id+"F6.wireOp",EDGE,"E51")])],"isStart":true}),makeQuery(id+"F7.opExtrude","CAP_FACE",FACE,{"disambiguationData":[OSD([sQuery(id+"F6.wireOp",EDGE,"E53.MirrorCS"),sQuery(id+"F6.wireOp",EDGE,"E54.MirrorCS"),sQuery(id+"F6.wireOp",EDGE,"E55.MirrorCS"),sQuery(id+"F6.wireOp",EDGE,"E56.MirrorCS")])],"isStart":true})]}),makeQuery(id+"F9.opExtrude","CAP_FACE",FACE,{"disambiguationData":[OSD([sQuery(id+"F8.wireOp",EDGE,"E57.0"),sQuery(id+"F8.wireOp",EDGE,"E58"),sQuery(id+"F8.wireOp",EDGE,"E59"),sQuery(id+"F8.wireOp",EDGE,"E60")])],"isStart":true}),makeQuery(id+"F9.opExtrude","CAP_FACE",FACE,{"disambiguationData":[OSD([sQuery(id+"F8.wireOp",EDGE,"E67.MirrorCS"),sQuery(id+"F8.wireOp",EDGE,"E68.MirrorCS"),sQuery(id+"F8.wireOp",EDGE,"E69.MirrorCS"),sQuery(id+"F8.wireOp",EDGE,"E70.MirrorCS")])],"isStart":true})]}),makeQuery(id+"F11.opExtrude","CAP_FACE",FACE,{"disambiguationData":[OSD([sQuery(id+"F10.wireOp",EDGE,"E72.0"),sQuery(id+"F10.wireOp",EDGE,"E74"),sQuery(id+"F10.wireOp",EDGE,"E76"),sQuery(id+"F10.wireOp",EDGE,"E77"),sQuery(id+"F10.wireOp",EDGE,"E80")])],"isStart":false}),makeQuery(id+"F11.opExtrude","CAP_FACE",FACE,{"disambiguationData":[OSD([sQuery(id+"F10.wireOp",EDGE,"E82.MirrorCS"),sQuery(id+"F10.wireOp",EDGE,"E83.MirrorCS"),sQuery(id+"F10.wireOp",EDGE,"E84.MirrorCS"),sQuery(id+"F10.wireOp",EDGE,"E85.MirrorCS"),sQuery(id+"F10.wireOp",EDGE,"E86.MirrorCS")])],"isStart":false})]}),makeQuery(id+"F20.opExtrude","CAP_FACE",FACE,{"disambiguationData":[OSD([sQuery(id+"F19.wireOp",EDGE,"E119.0"),sQuery(id+"F19.wireOp",EDGE,"E120.0"),sQuery(id+"F19.wireOp",EDGE,"E121.0"),sQuery(id+"F19.wireOp",EDGE,"E122")])],"isStart":true})]});
            var sketch = newSketch(context, id + "F23", { "sketchPlane" : qUnion([Q0])});
            skCircle(sketch, "E127.0", {"center": v(-3.87, -22.09) * mm, "radius": 1.5 * mm, "construction": true});
            skLineSegment(sketch, "E128", {"start": v(-3.87, -22.09) * mm, "end": v(-3.87, -15.14) * mm, "construction": true});
            skCircle(sketch, "E129", {"center": v(-3.87, -15.14) * mm, "radius": 1.5 * mm});
            skCircle(sketch, "E130.0", {"center": v(-3.87, -22.09) * mm, "radius": 2.8 * mm, "construction": true});
            skArc(sketch, "E131.0", {"start": v(-7.81, -22.78) * mm, "mid": v(-4.57, -18.15) * mm, "end": v(0.06, -21.4) * mm, "construction": true});
            skCircle(sketch, "E132", {"center": v(-3.87, -15.14) * mm, "radius": 2.8 * mm, "construction": true});
            skArc(sketch, "E133", {"start": v(0.12, -14.9) * mm, "mid": v(-4, -11.14) * mm, "end": v(-7.87, -15.14) * mm});
            skLineSegment(sketch, "E134", {"start": v(0.12, -14.9) * mm, "end": v(0.76, -25.33) * mm});
            skLineSegment(sketch, "E135", {"start": v(-7.87, -15.14) * mm, "end": v(-7.87, -22.44) * mm});
            skLineSegment(sketch, "E136", {"start": v(0.76, -25.33) * mm, "end": v(-7.28, -25.83) * mm});
            skLineSegment(sketch, "E137", {"start": v(-7.28, -25.83) * mm, "end": v(-7.81, -22.78) * mm});
            skLineSegment(sketch, "E138", {"start": v(-7.81, -22.78) * mm, "end": v(-7.87, -22.44) * mm});
            skSolve(sketch);
        }
        {
            var Q0;
            Q0 = qSketchRegion(id + "F23", true);
            var Q1;
            {var subQ0=sQuery(id+"F2.wireOp",EDGE,"E20.0");var subQ1=sQuery(id+"F2.wireOp",EDGE,"E19.0");var subQ2=sQuery(id+"F2.wireOp",EDGE,"E21.0");var subQ3=sQuery(id+"F2.wireOp",EDGE,"E22.0");var subQ4=sQuery(id+"F2.wireOp",EDGE,"E23.0");var subQ5=sQuery(id+"F2.wireOp",EDGE,"E34");var subQ6=sQuery(id+"F2.wireOp",EDGE,"E30");var subQ7=sQuery(id+"F2.wireOp",EDGE,"E29");var subQ8=sQuery(id+"F2.wireOp",EDGE,"E33");var subQ9=sQuery(id+"F2.wireOp",EDGE,"E32");var subQ10=sQuery(id+"F2.wireOp",EDGE,"E31");Q1=makeQuery(id+"F22.boolean.opBoolean","MERGE",FACE,{"derivedFrom":[makeQuery(id+"F11.boolean.opBoolean","MERGE",FACE,{"derivedFrom":[makeQuery(id+"F9.boolean.opBoolean","MERGE",FACE,{"derivedFrom":[makeQuery(id+"F7.boolean.opBoolean","MERGE",FACE,{"derivedFrom":[makeQuery(id+"F3.boolean.opBoolean","SPLIT",FACE,{"disambiguationData":[TD([makeQuery(id+"F1.opExtrude","SWEPT_FACE",FACE,{"disambiguationData":[OSD([sQuery(id+"F0.wireOp",EDGE,"E0")])]})])],"derivedFrom":makeQuery(id+"F3.opExtrude","CAP_FACE",FACE,{"disambiguationData":[OSD([subQ1,subQ0,subQ2,subQ3,subQ4,sQuery(id+"F2.wireOp",EDGE,"E24.0"),sQuery(id+"F2.wireOp",EDGE,"E25.0"),sQuery(id+"F2.wireOp",EDGE,"E26.0"),sQuery(id+"F2.wireOp",EDGE,"E27.0"),sQuery(id+"F2.wireOp",EDGE,"E28.0"),subQ7,subQ6,subQ10,subQ9,subQ8,subQ5])],"isStart":true})}),makeQuery(id+"F7.opExtrude","CAP_FACE",FACE,{"disambiguationData":[OSD([sQuery(id+"F6.wireOp",EDGE,"E53.MirrorCS"),sQuery(id+"F6.wireOp",EDGE,"E54.MirrorCS"),sQuery(id+"F6.wireOp",EDGE,"E55.MirrorCS"),sQuery(id+"F6.wireOp",EDGE,"E56.MirrorCS")])],"isStart":false})]}),makeQuery(id+"F9.opExtrude","CAP_FACE",FACE,{"disambiguationData":[OSD([sQuery(id+"F8.wireOp",EDGE,"E57.0"),sQuery(id+"F8.wireOp",EDGE,"E58"),sQuery(id+"F8.wireOp",EDGE,"E59"),sQuery(id+"F8.wireOp",EDGE,"E60")])],"isStart":false})]}),makeQuery(id+"F11.opExtrude","CAP_FACE",FACE,{"disambiguationData":[OSD([sQuery(id+"F10.wireOp",EDGE,"E82.MirrorCS"),sQuery(id+"F10.wireOp",EDGE,"E83.MirrorCS"),sQuery(id+"F10.wireOp",EDGE,"E84.MirrorCS"),sQuery(id+"F10.wireOp",EDGE,"E85.MirrorCS"),sQuery(id+"F10.wireOp",EDGE,"E86.MirrorCS")])],"isStart":true})]}),makeQuery(id+"F22.opExtrude","CAP_FACE",FACE,{"disambiguationData":[OSD([sQuery(id+"F21.wireOp",EDGE,"E123.0.4"),sQuery(id+"F21.wireOp",EDGE,"E123.0.5"),sQuery(id+"F21.wireOp",EDGE,"E123.0.6"),sQuery(id+"F21.wireOp",EDGE,"E123.0.7"),sQuery(id+"F21.wireOp",EDGE,"E123.0.8"),sQuery(id+"F21.wireOp",EDGE,"E123.0.9"),sQuery(id+"F21.wireOp",EDGE,"E124.1"),sQuery(id+"F21.wireOp",EDGE,"E124.5"),sQuery(id+"F21.wireOp",EDGE,"E124.7"),sQuery(id+"F21.wireOp",EDGE,"E124.8"),sQuery(id+"F21.wireOp",EDGE,"E124.9"),sQuery(id+"F21.wireOp",EDGE,"E126.trimOffspring")])],"isStart":false})]});}
            extrude(context, id + "F24", {"entities" : qUnion([Q0]), "operationType" : NewBodyOperationType.ADD, "endBound" : BoundingType.UP_TO_SURFACE, "oppositeDirection" : true, "endBoundEntityFace" : qUnion([Q1]), "depth" : 25 * mm});
        }
        {
            var Q0;
            Q0=makeQuery(id+"F24.boolean.opBoolean","MERGE",FACE,{"derivedFrom":[makeQuery(id+"F20.boolean.opBoolean","MERGE",FACE,{"derivedFrom":[makeQuery(id+"F11.boolean.opBoolean","MERGE",FACE,{"derivedFrom":[makeQuery(id+"F9.boolean.opBoolean","MERGE",FACE,{"derivedFrom":[makeQuery(id+"F7.boolean.opBoolean","MERGE",FACE,{"derivedFrom":[makeQuery(id+"F4.opExtrude","CAP_FACE",FACE,{"disambiguationData":[OSD([sQuery(id+"F2.wireOp",EDGE,"E19.0"),sQuery(id+"F2.wireOp",EDGE,"E20.0"),sQuery(id+"F2.wireOp",EDGE,"E21.0"),sQuery(id+"F2.wireOp",EDGE,"E22.0"),sQuery(id+"F2.wireOp",EDGE,"E23.0"),sQuery(id+"F2.wireOp",EDGE,"E24.0"),sQuery(id+"F2.wireOp",EDGE,"E25.0"),sQuery(id+"F2.wireOp",EDGE,"E26.0"),sQuery(id+"F2.wireOp",EDGE,"E27.0"),sQuery(id+"F2.wireOp",EDGE,"E28.0"),sQuery(id+"F2.wireOp",EDGE,"E29"),sQuery(id+"F2.wireOp",EDGE,"E30"),sQuery(id+"F2.wireOp",EDGE,"E31"),sQuery(id+"F2.wireOp",EDGE,"E32"),sQuery(id+"F2.wireOp",EDGE,"E33"),sQuery(id+"F2.wireOp",EDGE,"E34")])],"isStart":false}),makeQuery(id+"F7.opExtrude","CAP_FACE",FACE,{"disambiguationData":[OSD([sQuery(id+"F6.wireOp",EDGE,"E45.0"),sQuery(id+"F6.wireOp",EDGE,"E48"),sQuery(id+"F6.wireOp",EDGE,"E50"),sQuery(id+"F6.wireOp",EDGE,"E51")])],"isStart":true}),makeQuery(id+"F7.opExtrude","CAP_FACE",FACE,{"disambiguationData":[OSD([sQuery(id+"F6.wireOp",EDGE,"E53.MirrorCS"),sQuery(id+"F6.wireOp",EDGE,"E54.MirrorCS"),sQuery(id+"F6.wireOp",EDGE,"E55.MirrorCS"),sQuery(id+"F6.wireOp",EDGE,"E56.MirrorCS")])],"isStart":true})]}),makeQuery(id+"F9.opExtrude","CAP_FACE",FACE,{"disambiguationData":[OSD([sQuery(id+"F8.wireOp",EDGE,"E57.0"),sQuery(id+"F8.wireOp",EDGE,"E58"),sQuery(id+"F8.wireOp",EDGE,"E59"),sQuery(id+"F8.wireOp",EDGE,"E60")])],"isStart":true}),makeQuery(id+"F9.opExtrude","CAP_FACE",FACE,{"disambiguationData":[OSD([sQuery(id+"F8.wireOp",EDGE,"E67.MirrorCS"),sQuery(id+"F8.wireOp",EDGE,"E68.MirrorCS"),sQuery(id+"F8.wireOp",EDGE,"E69.MirrorCS"),sQuery(id+"F8.wireOp",EDGE,"E70.MirrorCS")])],"isStart":true})]}),makeQuery(id+"F11.opExtrude","CAP_FACE",FACE,{"disambiguationData":[OSD([sQuery(id+"F10.wireOp",EDGE,"E72.0"),sQuery(id+"F10.wireOp",EDGE,"E74"),sQuery(id+"F10.wireOp",EDGE,"E76"),sQuery(id+"F10.wireOp",EDGE,"E77"),sQuery(id+"F10.wireOp",EDGE,"E80")])],"isStart":false}),makeQuery(id+"F11.opExtrude","CAP_FACE",FACE,{"disambiguationData":[OSD([sQuery(id+"F10.wireOp",EDGE,"E82.MirrorCS"),sQuery(id+"F10.wireOp",EDGE,"E83.MirrorCS"),sQuery(id+"F10.wireOp",EDGE,"E84.MirrorCS"),sQuery(id+"F10.wireOp",EDGE,"E85.MirrorCS"),sQuery(id+"F10.wireOp",EDGE,"E86.MirrorCS")])],"isStart":false})]}),makeQuery(id+"F20.opExtrude","CAP_FACE",FACE,{"disambiguationData":[OSD([sQuery(id+"F19.wireOp",EDGE,"E119.0"),sQuery(id+"F19.wireOp",EDGE,"E120.0"),sQuery(id+"F19.wireOp",EDGE,"E121.0"),sQuery(id+"F19.wireOp",EDGE,"E122")])],"isStart":true})]}),makeQuery(id+"F24.opExtrude","CAP_FACE",FACE,{"disambiguationData":[OSD([sQuery(id+"F23.wireOp",EDGE,"E129"),sQuery(id+"F23.wireOp",EDGE,"E133"),sQuery(id+"F23.wireOp",EDGE,"E134"),sQuery(id+"F23.wireOp",EDGE,"E135"),sQuery(id+"F23.wireOp",EDGE,"E136"),sQuery(id+"F23.wireOp",EDGE,"E137"),sQuery(id+"F23.wireOp",EDGE,"E138")])],"isStart":true})]});
            var sketch = newSketch(context, id + "F25", { "sketchPlane" : qUnion([Q0])});
            skLineSegment(sketch, "E139", {"start": v(6.23, -56.35) * mm, "end": v(-10.54, -59.31) * mm});
            skLineSegment(sketch, "E140", {"start": v(-10.54, -59.31) * mm, "end": v(6.23, -72.6) * mm});
            skLineSegment(sketch, "E141", {"start": v(6.23, -72.6) * mm, "end": v(13.78, -68) * mm});
            skLineSegment(sketch, "E142", {"start": v(13.78, -68) * mm, "end": v(6.23, -56.35) * mm});
            skSolve(sketch);
        }
        {
            var Q0;
            Q0 = qSketchRegion(id + "F25", true);
            extrude(context, id + "F26", {"entities" : qUnion([Q0]), "operationType" : NewBodyOperationType.REMOVE, "oppositeDirection" : true, "depth" : 25 * mm});
        }
        {
            var Q0;
            Q0=makeQuery(id+"F24.boolean.opBoolean","MERGE",FACE,{"derivedFrom":[makeQuery(id+"F20.boolean.opBoolean","MERGE",FACE,{"derivedFrom":[makeQuery(id+"F11.boolean.opBoolean","MERGE",FACE,{"derivedFrom":[makeQuery(id+"F9.boolean.opBoolean","MERGE",FACE,{"derivedFrom":[makeQuery(id+"F7.boolean.opBoolean","MERGE",FACE,{"derivedFrom":[makeQuery(id+"F4.opExtrude","CAP_FACE",FACE,{"disambiguationData":[OSD([sQuery(id+"F2.wireOp",EDGE,"E19.0"),sQuery(id+"F2.wireOp",EDGE,"E20.0"),sQuery(id+"F2.wireOp",EDGE,"E21.0"),sQuery(id+"F2.wireOp",EDGE,"E22.0"),sQuery(id+"F2.wireOp",EDGE,"E23.0"),sQuery(id+"F2.wireOp",EDGE,"E24.0"),sQuery(id+"F2.wireOp",EDGE,"E25.0"),sQuery(id+"F2.wireOp",EDGE,"E26.0"),sQuery(id+"F2.wireOp",EDGE,"E27.0"),sQuery(id+"F2.wireOp",EDGE,"E28.0"),sQuery(id+"F2.wireOp",EDGE,"E29"),sQuery(id+"F2.wireOp",EDGE,"E30"),sQuery(id+"F2.wireOp",EDGE,"E31"),sQuery(id+"F2.wireOp",EDGE,"E32"),sQuery(id+"F2.wireOp",EDGE,"E33"),sQuery(id+"F2.wireOp",EDGE,"E34")])],"isStart":false}),makeQuery(id+"F7.opExtrude","CAP_FACE",FACE,{"disambiguationData":[OSD([sQuery(id+"F6.wireOp",EDGE,"E45.0"),sQuery(id+"F6.wireOp",EDGE,"E48"),sQuery(id+"F6.wireOp",EDGE,"E50"),sQuery(id+"F6.wireOp",EDGE,"E51")])],"isStart":true}),makeQuery(id+"F7.opExtrude","CAP_FACE",FACE,{"disambiguationData":[OSD([sQuery(id+"F6.wireOp",EDGE,"E53.MirrorCS"),sQuery(id+"F6.wireOp",EDGE,"E54.MirrorCS"),sQuery(id+"F6.wireOp",EDGE,"E55.MirrorCS"),sQuery(id+"F6.wireOp",EDGE,"E56.MirrorCS")])],"isStart":true})]}),makeQuery(id+"F9.opExtrude","CAP_FACE",FACE,{"disambiguationData":[OSD([sQuery(id+"F8.wireOp",EDGE,"E57.0"),sQuery(id+"F8.wireOp",EDGE,"E58"),sQuery(id+"F8.wireOp",EDGE,"E59"),sQuery(id+"F8.wireOp",EDGE,"E60")])],"isStart":true}),makeQuery(id+"F9.opExtrude","CAP_FACE",FACE,{"disambiguationData":[OSD([sQuery(id+"F8.wireOp",EDGE,"E67.MirrorCS"),sQuery(id+"F8.wireOp",EDGE,"E68.MirrorCS"),sQuery(id+"F8.wireOp",EDGE,"E69.MirrorCS"),sQuery(id+"F8.wireOp",EDGE,"E70.MirrorCS")])],"isStart":true})]}),makeQuery(id+"F11.opExtrude","CAP_FACE",FACE,{"disambiguationData":[OSD([sQuery(id+"F10.wireOp",EDGE,"E72.0"),sQuery(id+"F10.wireOp",EDGE,"E74"),sQuery(id+"F10.wireOp",EDGE,"E76"),sQuery(id+"F10.wireOp",EDGE,"E77"),sQuery(id+"F10.wireOp",EDGE,"E80")])],"isStart":false}),makeQuery(id+"F11.opExtrude","CAP_FACE",FACE,{"disambiguationData":[OSD([sQuery(id+"F10.wireOp",EDGE,"E82.MirrorCS"),sQuery(id+"F10.wireOp",EDGE,"E83.MirrorCS"),sQuery(id+"F10.wireOp",EDGE,"E84.MirrorCS"),sQuery(id+"F10.wireOp",EDGE,"E85.MirrorCS"),sQuery(id+"F10.wireOp",EDGE,"E86.MirrorCS")])],"isStart":false})]}),makeQuery(id+"F20.opExtrude","CAP_FACE",FACE,{"disambiguationData":[OSD([sQuery(id+"F19.wireOp",EDGE,"E119.0"),sQuery(id+"F19.wireOp",EDGE,"E120.0"),sQuery(id+"F19.wireOp",EDGE,"E121.0"),sQuery(id+"F19.wireOp",EDGE,"E122")])],"isStart":true})]}),makeQuery(id+"F24.opExtrude","CAP_FACE",FACE,{"disambiguationData":[OSD([sQuery(id+"F23.wireOp",EDGE,"E129"),sQuery(id+"F23.wireOp",EDGE,"E133"),sQuery(id+"F23.wireOp",EDGE,"E134"),sQuery(id+"F23.wireOp",EDGE,"E135"),sQuery(id+"F23.wireOp",EDGE,"E136"),sQuery(id+"F23.wireOp",EDGE,"E137"),sQuery(id+"F23.wireOp",EDGE,"E138")])],"isStart":true})]});
            var sketch = newSketch(context, id + "F27", { "sketchPlane" : qUnion([Q0])});
            skLineSegment(sketch, "E143.0", {"start": v(-22.5, 71.13) * mm, "end": v(-22.5, 67.1) * mm});
            skLineSegment(sketch, "E144.0", {"start": v(-28, 71.13) * mm, "end": v(-28, 67.1) * mm});
            skArc(sketch, "E145.0", {"start": v(-28, 67.1) * mm, "mid": v(-26.83, 59.07) * mm, "end": v(-23.4, 51.73) * mm});
            skLineSegment(sketch, "E146.0", {"start": v(85.29, 23.63) * mm, "end": v(65.59, 27.1) * mm});
            skLineSegment(sketch, "E147.0", {"start": v(11.4, 42.24) * mm, "end": v(31.1, 38.77) * mm});
            skArc(sketch, "E148.0", {"start": v(94.57, -27.57) * mm, "mid": v(102.28, -25.02) * mm, "end": v(108.93, -20.36) * mm});
            skArc(sketch, "E149.0", {"start": v(93.62, -22.16) * mm, "mid": v(99.81, -20.1) * mm, "end": v(105.15, -16.36) * mm});
            skLineSegment(sketch, "E150.0", {"start": v(86.7, -28.96) * mm, "end": v(67, -32.44) * mm});
            skLineSegment(sketch, "E151.0", {"start": v(85.74, -23.55) * mm, "end": v(66.04, -27.02) * mm});
            skArc(sketch, "E152.0", {"start": v(-22.5, 67.1) * mm, "mid": v(-21.56, 60.65) * mm, "end": v(-18.8, 54.74) * mm});
            skLineSegment(sketch, "E153", {"start": v(-4.86, 39.52) * mm, "end": v(2.56, 38.21) * mm});
            skLineSegment(sketch, "E154", {"start": v(-3.9, 44.94) * mm, "end": v(3.52, 43.63) * mm});
            skLineSegment(sketch, "E155", {"start": v(-18.8, 54.74) * mm, "end": v(-23.4, 51.73) * mm});
            skLineSegment(sketch, "E156", {"start": v(-13.6, 49.18) * mm, "end": v(-16.93, 44.8) * mm});
            skLineSegment(sketch, "E157", {"start": v(2.56, 38.21) * mm, "end": v(3.52, 43.63) * mm});
            skLineSegment(sketch, "E158", {"start": v(11.4, 42.24) * mm, "end": v(10.44, 36.82) * mm});
            skLineSegment(sketch, "E159", {"start": v(-28, 71.13) * mm, "end": v(-22.5, 71.13) * mm});
            skLineSegment(sketch, "E160", {"start": v(31.1, 38.77) * mm, "end": v(30.14, 33.35) * mm});
            skLineSegment(sketch, "E161", {"start": v(38.97, 37.38) * mm, "end": v(38.01, 31.96) * mm});
            skLineSegment(sketch, "E162", {"start": v(58.67, 33.9) * mm, "end": v(57.71, 28.49) * mm});
            skLineSegment(sketch, "E163", {"start": v(66.54, 32.52) * mm, "end": v(65.59, 27.1) * mm});
            skLineSegment(sketch, "E164", {"start": v(86.24, 29.04) * mm, "end": v(85.29, 23.63) * mm});
            skLineSegment(sketch, "E165", {"start": v(94.57, 27.57) * mm, "end": v(93.62, 22.16) * mm});
            skLineSegment(sketch, "E166", {"start": v(109.9, 9.92) * mm, "end": v(114.84, 12.34) * mm});
            skLineSegment(sketch, "E167", {"start": v(111.9, 3.73) * mm, "end": v(117.32, 4.64) * mm});
            skLineSegment(sketch, "E168", {"start": v(109.19, -11.27) * mm, "end": v(113.95, -14.02) * mm});
            skLineSegment(sketch, "E169", {"start": v(105.15, -16.36) * mm, "end": v(108.93, -20.36) * mm});
            skLineSegment(sketch, "E170", {"start": v(10.9, -36.74) * mm, "end": v(11.85, -42.16) * mm});
            skLineSegment(sketch, "E171", {"start": v(30.6, -33.27) * mm, "end": v(31.55, -38.69) * mm});
            skLineSegment(sketch, "E172", {"start": v(38.47, -31.88) * mm, "end": v(39.42, -37.3) * mm});
            skLineSegment(sketch, "E173", {"start": v(58.17, -28.4) * mm, "end": v(59.12, -33.83) * mm});
            skLineSegment(sketch, "E174", {"start": v(66.04, -27.02) * mm, "end": v(67, -32.44) * mm});
            skLineSegment(sketch, "E175", {"start": v(85.74, -23.55) * mm, "end": v(86.7, -28.96) * mm});
            skLineSegment(sketch, "E176", {"start": v(93.62, -22.16) * mm, "end": v(94.57, -27.57) * mm});
            skLineSegment(sketch, "E177.trimOffspring", {"start": v(30.6, -33.27) * mm, "end": v(10.9, -36.74) * mm});
            skLineSegment(sketch, "E178.trimOffspring", {"start": v(31.55, -38.69) * mm, "end": v(11.85, -42.16) * mm});
            skLineSegment(sketch, "E179.trimOffspring", {"start": v(58.17, -28.4) * mm, "end": v(38.47, -31.88) * mm});
            skLineSegment(sketch, "E180.trimOffspring", {"start": v(59.12, -33.83) * mm, "end": v(39.42, -37.3) * mm});
            skArc(sketch, "E181.trimOffspring", {"start": v(113.95, -14.02) * mm, "mid": v(117.26, -4.98) * mm, "end": v(117.32, 4.64) * mm});
            skArc(sketch, "E182.trimOffspring", {"start": v(109.19, -11.27) * mm, "mid": v(111.85, -4) * mm, "end": v(111.9, 3.73) * mm});
            skArc(sketch, "E183.trimOffspring", {"start": v(109.9, 9.92) * mm, "mid": v(103.23, 17.99) * mm, "end": v(93.62, 22.16) * mm});
            skArc(sketch, "E184.trimOffspring", {"start": v(114.84, 12.34) * mm, "mid": v(106.53, 22.39) * mm, "end": v(94.57, 27.57) * mm});
            skLineSegment(sketch, "E185.trimOffspring", {"start": v(66.54, 32.52) * mm, "end": v(86.24, 29.04) * mm});
            skLineSegment(sketch, "E186.trimOffspring", {"start": v(57.71, 28.49) * mm, "end": v(38.01, 31.96) * mm});
            skLineSegment(sketch, "E187.trimOffspring", {"start": v(38.97, 37.38) * mm, "end": v(58.67, 33.9) * mm});
            skLineSegment(sketch, "E188.trimOffspring", {"start": v(30.14, 33.35) * mm, "end": v(10.44, 36.82) * mm});
            skArc(sketch, "E189.trimOffspring", {"start": v(-13.6, 49.18) * mm, "mid": v(-9.01, 46.48) * mm, "end": v(-3.9, 44.94) * mm});
            skArc(sketch, "E190.trimOffspring", {"start": v(-16.93, 44.8) * mm, "mid": v(-11.21, 41.44) * mm, "end": v(-4.86, 39.52) * mm});
            skLineSegment(sketch, "E191", {"start": v(86.24, 29.04) * mm, "end": v(94.57, 27.57) * mm, "construction": true});
            skLineSegment(sketch, "E192", {"start": v(85.29, 23.63) * mm, "end": v(93.62, 22.16) * mm, "construction": true});
            skSolve(sketch);
        }
        {
            var Q0;
            Q0 = qSketchRegion(id + "F27", true);
            extrude(context, id + "F28", {"entities" : qUnion([Q0]), "operationType" : NewBodyOperationType.REMOVE, "oppositeDirection" : true, "depth" : 25 * mm});
        }
        {
            var Q0;
            Q0=makeQuery(id+"F28.boolean.opBoolean","COPY",EDGE,{"derivedFrom":makeQuery(id+"F28.opExtrude","SWEPT_EDGE",EDGE,{"disambiguationData":[OSD([sQuery(id+"F27.wireOp",EDGE,"E153"),sQuery(id+"F27.wireOp",EDGE,"E157")])]})});
            var Q1;
            Q1=makeQuery(id+"F28.boolean.opBoolean","COPY",EDGE,{"derivedFrom":makeQuery(id+"F28.opExtrude","SWEPT_EDGE",EDGE,{"disambiguationData":[OSD([sQuery(id+"F27.wireOp",EDGE,"E154"),sQuery(id+"F27.wireOp",EDGE,"E157")])]})});
            var Q2;
            Q2=makeQuery(id+"F28.boolean.opBoolean","COPY",EDGE,{"derivedFrom":makeQuery(id+"F28.opExtrude","SWEPT_EDGE",EDGE,{"disambiguationData":[OSD([sQuery(id+"F27.wireOp",EDGE,"E156"),sQuery(id+"F27.wireOp",EDGE,"E189.trimOffspring")])]})});
            var Q3;
            Q3=makeQuery(id+"F28.boolean.opBoolean","COPY",EDGE,{"derivedFrom":makeQuery(id+"F28.opExtrude","SWEPT_EDGE",EDGE,{"disambiguationData":[OSD([sQuery(id+"F27.wireOp",EDGE,"E156"),sQuery(id+"F27.wireOp",EDGE,"E190.trimOffspring")])]})});
            var Q4;
            Q4=makeQuery(id+"F28.boolean.opBoolean","COPY",EDGE,{"derivedFrom":makeQuery(id+"F28.opExtrude","SWEPT_EDGE",EDGE,{"disambiguationData":[OSD([sQuery(id+"F27.wireOp",EDGE,"E144.0"),sQuery(id+"F27.wireOp",EDGE,"E159")])]})});
            var Q5;
            Q5=makeQuery(id+"F28.boolean.opBoolean","COPY",EDGE,{"derivedFrom":makeQuery(id+"F28.opExtrude","SWEPT_EDGE",EDGE,{"disambiguationData":[OSD([sQuery(id+"F27.wireOp",EDGE,"E143.0"),sQuery(id+"F27.wireOp",EDGE,"E159")])]})});
            var Q6;
            Q6=makeQuery(id+"F28.boolean.opBoolean","COPY",EDGE,{"derivedFrom":makeQuery(id+"F28.opExtrude","SWEPT_EDGE",EDGE,{"disambiguationData":[OSD([sQuery(id+"F27.wireOp",EDGE,"E152.0"),sQuery(id+"F27.wireOp",EDGE,"E155")])]})});
            var Q7;
            Q7=makeQuery(id+"F28.boolean.opBoolean","COPY",EDGE,{"derivedFrom":makeQuery(id+"F28.opExtrude","SWEPT_EDGE",EDGE,{"disambiguationData":[OSD([sQuery(id+"F27.wireOp",EDGE,"E145.0"),sQuery(id+"F27.wireOp",EDGE,"E155")])]})});
            var Q8;
            Q8=makeQuery(id+"F28.boolean.opBoolean","COPY",EDGE,{"derivedFrom":makeQuery(id+"F28.opExtrude","SWEPT_EDGE",EDGE,{"disambiguationData":[OSD([sQuery(id+"F27.wireOp",EDGE,"E158"),sQuery(id+"F27.wireOp",EDGE,"E188.trimOffspring")])]})});
            var Q9;
            Q9=makeQuery(id+"F28.boolean.opBoolean","COPY",EDGE,{"derivedFrom":makeQuery(id+"F28.opExtrude","SWEPT_EDGE",EDGE,{"disambiguationData":[OSD([sQuery(id+"F27.wireOp",EDGE,"E147.0"),sQuery(id+"F27.wireOp",EDGE,"E158")])]})});
            var Q10;
            Q10=makeQuery(id+"F28.boolean.opBoolean","COPY",EDGE,{"derivedFrom":makeQuery(id+"F28.opExtrude","SWEPT_EDGE",EDGE,{"disambiguationData":[OSD([sQuery(id+"F27.wireOp",EDGE,"E162"),sQuery(id+"F27.wireOp",EDGE,"E187.trimOffspring")])]})});
            var Q11;
            Q11=makeQuery(id+"F28.boolean.opBoolean","COPY",EDGE,{"derivedFrom":makeQuery(id+"F28.opExtrude","SWEPT_EDGE",EDGE,{"disambiguationData":[OSD([sQuery(id+"F27.wireOp",EDGE,"E162"),sQuery(id+"F27.wireOp",EDGE,"E186.trimOffspring")])]})});
            var Q12;
            Q12=makeQuery(id+"F28.boolean.opBoolean","COPY",EDGE,{"derivedFrom":makeQuery(id+"F28.opExtrude","SWEPT_EDGE",EDGE,{"disambiguationData":[OSD([sQuery(id+"F27.wireOp",EDGE,"E146.0"),sQuery(id+"F27.wireOp",EDGE,"E164")])]})});
            var Q13;
            Q13=makeQuery(id+"F28.boolean.opBoolean","COPY",EDGE,{"derivedFrom":makeQuery(id+"F28.opExtrude","SWEPT_EDGE",EDGE,{"disambiguationData":[OSD([sQuery(id+"F27.wireOp",EDGE,"E164"),sQuery(id+"F27.wireOp",EDGE,"E185.trimOffspring")])]})});
            var Q14;
            Q14=makeQuery(id+"F28.boolean.opBoolean","COPY",EDGE,{"derivedFrom":makeQuery(id+"F28.opExtrude","SWEPT_EDGE",EDGE,{"disambiguationData":[OSD([sQuery(id+"F27.wireOp",EDGE,"E163"),sQuery(id+"F27.wireOp",EDGE,"E185.trimOffspring")])]})});
            var Q15;
            Q15=makeQuery(id+"F28.boolean.opBoolean","COPY",EDGE,{"derivedFrom":makeQuery(id+"F28.opExtrude","SWEPT_EDGE",EDGE,{"disambiguationData":[OSD([sQuery(id+"F27.wireOp",EDGE,"E146.0"),sQuery(id+"F27.wireOp",EDGE,"E163")])]})});
            var Q16;
            Q16=makeQuery(id+"F28.boolean.opBoolean","COPY",EDGE,{"derivedFrom":makeQuery(id+"F28.opExtrude","SWEPT_EDGE",EDGE,{"disambiguationData":[OSD([sQuery(id+"F27.wireOp",EDGE,"E165"),sQuery(id+"F27.wireOp",EDGE,"E183.trimOffspring")])]})});
            var Q17;
            Q17=makeQuery(id+"F28.boolean.opBoolean","COPY",EDGE,{"derivedFrom":makeQuery(id+"F28.opExtrude","SWEPT_EDGE",EDGE,{"disambiguationData":[OSD([sQuery(id+"F27.wireOp",EDGE,"E165"),sQuery(id+"F27.wireOp",EDGE,"E184.trimOffspring")])]})});
            var Q18;
            Q18=makeQuery(id+"F28.boolean.opBoolean","COPY",EDGE,{"derivedFrom":makeQuery(id+"F28.opExtrude","SWEPT_EDGE",EDGE,{"disambiguationData":[OSD([sQuery(id+"F27.wireOp",EDGE,"E167"),sQuery(id+"F27.wireOp",EDGE,"E182.trimOffspring")])]})});
            var Q19;
            Q19=makeQuery(id+"F28.boolean.opBoolean","COPY",EDGE,{"derivedFrom":makeQuery(id+"F28.opExtrude","SWEPT_EDGE",EDGE,{"disambiguationData":[OSD([sQuery(id+"F27.wireOp",EDGE,"E168"),sQuery(id+"F27.wireOp",EDGE,"E182.trimOffspring")])]})});
            var Q20;
            Q20=makeQuery(id+"F28.boolean.opBoolean","COPY",EDGE,{"derivedFrom":makeQuery(id+"F28.opExtrude","SWEPT_EDGE",EDGE,{"disambiguationData":[OSD([sQuery(id+"F27.wireOp",EDGE,"E149.0"),sQuery(id+"F27.wireOp",EDGE,"E176")])]})});
            var Q21;
            Q21=makeQuery(id+"F28.boolean.opBoolean","COPY",EDGE,{"derivedFrom":makeQuery(id+"F28.opExtrude","SWEPT_EDGE",EDGE,{"disambiguationData":[OSD([sQuery(id+"F27.wireOp",EDGE,"E149.0"),sQuery(id+"F27.wireOp",EDGE,"E169")])]})});
            var Q22;
            Q22=makeQuery(id+"F28.boolean.opBoolean","COPY",EDGE,{"derivedFrom":makeQuery(id+"F28.opExtrude","SWEPT_EDGE",EDGE,{"disambiguationData":[OSD([sQuery(id+"F27.wireOp",EDGE,"E151.0"),sQuery(id+"F27.wireOp",EDGE,"E175")])]})});
            var Q23;
            Q23=makeQuery(id+"F28.boolean.opBoolean","COPY",EDGE,{"derivedFrom":makeQuery(id+"F28.opExtrude","SWEPT_EDGE",EDGE,{"disambiguationData":[OSD([sQuery(id+"F27.wireOp",EDGE,"E151.0"),sQuery(id+"F27.wireOp",EDGE,"E174")])]})});
            var Q24;
            Q24=makeQuery(id+"F28.boolean.opBoolean","COPY",EDGE,{"derivedFrom":makeQuery(id+"F28.opExtrude","SWEPT_EDGE",EDGE,{"disambiguationData":[OSD([sQuery(id+"F27.wireOp",EDGE,"E173"),sQuery(id+"F27.wireOp",EDGE,"E179.trimOffspring")])]})});
            var Q25;
            Q25=makeQuery(id+"F28.boolean.opBoolean","COPY",EDGE,{"derivedFrom":makeQuery(id+"F28.opExtrude","SWEPT_EDGE",EDGE,{"disambiguationData":[OSD([sQuery(id+"F27.wireOp",EDGE,"E172"),sQuery(id+"F27.wireOp",EDGE,"E179.trimOffspring")])]})});
            var Q26;
            Q26=makeQuery(id+"F28.boolean.opBoolean","COPY",EDGE,{"derivedFrom":makeQuery(id+"F28.opExtrude","SWEPT_EDGE",EDGE,{"disambiguationData":[OSD([sQuery(id+"F27.wireOp",EDGE,"E170"),sQuery(id+"F27.wireOp",EDGE,"E177.trimOffspring")])]})});
            var Q27;
            Q27=makeQuery(id+"F28.boolean.opBoolean","COPY",EDGE,{"derivedFrom":makeQuery(id+"F28.opExtrude","SWEPT_EDGE",EDGE,{"disambiguationData":[OSD([sQuery(id+"F27.wireOp",EDGE,"E171"),sQuery(id+"F27.wireOp",EDGE,"E177.trimOffspring")])]})});
            var Q28;
            Q28=makeQuery(id+"F28.boolean.opBoolean","COPY",EDGE,{"derivedFrom":makeQuery(id+"F28.opExtrude","SWEPT_EDGE",EDGE,{"disambiguationData":[OSD([sQuery(id+"F27.wireOp",EDGE,"E170"),sQuery(id+"F27.wireOp",EDGE,"E178.trimOffspring")])]})});
            var Q29;
            Q29=makeQuery(id+"F28.boolean.opBoolean","COPY",EDGE,{"derivedFrom":makeQuery(id+"F28.opExtrude","SWEPT_EDGE",EDGE,{"disambiguationData":[OSD([sQuery(id+"F27.wireOp",EDGE,"E171"),sQuery(id+"F27.wireOp",EDGE,"E178.trimOffspring")])]})});
            var Q30;
            Q30=makeQuery(id+"F28.boolean.opBoolean","COPY",EDGE,{"derivedFrom":makeQuery(id+"F28.opExtrude","SWEPT_EDGE",EDGE,{"disambiguationData":[OSD([sQuery(id+"F27.wireOp",EDGE,"E173"),sQuery(id+"F27.wireOp",EDGE,"E180.trimOffspring")])]})});
            var Q31;
            Q31=makeQuery(id+"F28.boolean.opBoolean","COPY",EDGE,{"derivedFrom":makeQuery(id+"F28.opExtrude","SWEPT_EDGE",EDGE,{"disambiguationData":[OSD([sQuery(id+"F27.wireOp",EDGE,"E150.0"),sQuery(id+"F27.wireOp",EDGE,"E175")])]})});
            var Q32;
            Q32=makeQuery(id+"F28.boolean.opBoolean","COPY",EDGE,{"derivedFrom":makeQuery(id+"F28.opExtrude","SWEPT_EDGE",EDGE,{"disambiguationData":[OSD([sQuery(id+"F27.wireOp",EDGE,"E148.0"),sQuery(id+"F27.wireOp",EDGE,"E169")])]})});
            var Q33;
            Q33=makeQuery(id+"F28.boolean.opBoolean","COPY",EDGE,{"derivedFrom":makeQuery(id+"F28.opExtrude","SWEPT_EDGE",EDGE,{"disambiguationData":[OSD([sQuery(id+"F27.wireOp",EDGE,"E172"),sQuery(id+"F27.wireOp",EDGE,"E180.trimOffspring")])]})});
            var Q34;
            Q34=makeQuery(id+"F28.boolean.opBoolean","COPY",EDGE,{"derivedFrom":makeQuery(id+"F28.opExtrude","SWEPT_EDGE",EDGE,{"disambiguationData":[OSD([sQuery(id+"F27.wireOp",EDGE,"E150.0"),sQuery(id+"F27.wireOp",EDGE,"E174")])]})});
            var Q35;
            Q35=makeQuery(id+"F28.boolean.opBoolean","COPY",EDGE,{"derivedFrom":makeQuery(id+"F28.opExtrude","SWEPT_EDGE",EDGE,{"disambiguationData":[OSD([sQuery(id+"F27.wireOp",EDGE,"E148.0"),sQuery(id+"F27.wireOp",EDGE,"E176")])]})});
            var Q36;
            Q36=makeQuery(id+"F28.boolean.opBoolean","COPY",EDGE,{"derivedFrom":makeQuery(id+"F28.opExtrude","SWEPT_EDGE",EDGE,{"disambiguationData":[OSD([sQuery(id+"F27.wireOp",EDGE,"E168"),sQuery(id+"F27.wireOp",EDGE,"E181.trimOffspring")])]})});
            var Q37;
            Q37=makeQuery(id+"F28.boolean.opBoolean","COPY",EDGE,{"derivedFrom":makeQuery(id+"F28.opExtrude","SWEPT_EDGE",EDGE,{"disambiguationData":[OSD([sQuery(id+"F27.wireOp",EDGE,"E167"),sQuery(id+"F27.wireOp",EDGE,"E181.trimOffspring")])]})});
            var Q38;
            Q38=makeQuery(id+"F28.boolean.opBoolean","COPY",EDGE,{"derivedFrom":makeQuery(id+"F28.opExtrude","SWEPT_EDGE",EDGE,{"disambiguationData":[OSD([sQuery(id+"F27.wireOp",EDGE,"E166"),sQuery(id+"F27.wireOp",EDGE,"E184.trimOffspring")])]})});
            var Q39;
            Q39=makeQuery(id+"F28.boolean.opBoolean","COPY",EDGE,{"derivedFrom":makeQuery(id+"F28.opExtrude","SWEPT_EDGE",EDGE,{"disambiguationData":[OSD([sQuery(id+"F27.wireOp",EDGE,"E166"),sQuery(id+"F27.wireOp",EDGE,"E183.trimOffspring")])]})});
            var Q40;
            Q40=makeQuery(id+"F28.boolean.opBoolean","COPY",EDGE,{"derivedFrom":makeQuery(id+"F28.opExtrude","SWEPT_EDGE",EDGE,{"disambiguationData":[OSD([sQuery(id+"F27.wireOp",EDGE,"E161"),sQuery(id+"F27.wireOp",EDGE,"E186.trimOffspring")])]})});
            var Q41;
            Q41=makeQuery(id+"F28.boolean.opBoolean","COPY",EDGE,{"derivedFrom":makeQuery(id+"F28.opExtrude","SWEPT_EDGE",EDGE,{"disambiguationData":[OSD([sQuery(id+"F27.wireOp",EDGE,"E160"),sQuery(id+"F27.wireOp",EDGE,"E188.trimOffspring")])]})});
            var Q42;
            Q42=makeQuery(id+"F28.boolean.opBoolean","COPY",EDGE,{"derivedFrom":makeQuery(id+"F28.opExtrude","SWEPT_EDGE",EDGE,{"disambiguationData":[OSD([sQuery(id+"F27.wireOp",EDGE,"E147.0"),sQuery(id+"F27.wireOp",EDGE,"E160")])]})});
            var Q43;
            Q43=makeQuery(id+"F28.boolean.opBoolean","COPY",EDGE,{"derivedFrom":makeQuery(id+"F28.opExtrude","SWEPT_EDGE",EDGE,{"disambiguationData":[OSD([sQuery(id+"F27.wireOp",EDGE,"E161"),sQuery(id+"F27.wireOp",EDGE,"E187.trimOffspring")])]})});
            fillet(context, id + "F29", {"entities" : qUnion([Q0, Q1, Q2, Q3, Q4, Q5, Q6, Q7, Q8, Q9, Q10, Q11, Q12, Q13, Q14, Q15, Q16, Q17, Q18, Q19, Q20, Q21, Q22, Q23, Q24, Q25, Q26, Q27, Q28, Q29, Q30, Q31, Q32, Q33, Q34, Q35, Q36, Q37, Q38, Q39, Q40, Q41, Q42, Q43]), "radius" : 3 * mm, "tangentPropagation" : true, "allowEdgeOverflow" : false});
        }
        {
            var Q0;
            Q0=makeQuery(id+"F24.boolean.opBoolean","MERGE",FACE,{"derivedFrom":[makeQuery(id+"F20.boolean.opBoolean","MERGE",FACE,{"derivedFrom":[makeQuery(id+"F11.boolean.opBoolean","MERGE",FACE,{"derivedFrom":[makeQuery(id+"F9.boolean.opBoolean","MERGE",FACE,{"derivedFrom":[makeQuery(id+"F7.boolean.opBoolean","MERGE",FACE,{"derivedFrom":[makeQuery(id+"F4.opExtrude","CAP_FACE",FACE,{"disambiguationData":[OSD([sQuery(id+"F2.wireOp",EDGE,"E19.0"),sQuery(id+"F2.wireOp",EDGE,"E20.0"),sQuery(id+"F2.wireOp",EDGE,"E21.0"),sQuery(id+"F2.wireOp",EDGE,"E22.0"),sQuery(id+"F2.wireOp",EDGE,"E23.0"),sQuery(id+"F2.wireOp",EDGE,"E24.0"),sQuery(id+"F2.wireOp",EDGE,"E25.0"),sQuery(id+"F2.wireOp",EDGE,"E26.0"),sQuery(id+"F2.wireOp",EDGE,"E27.0"),sQuery(id+"F2.wireOp",EDGE,"E28.0"),sQuery(id+"F2.wireOp",EDGE,"E29"),sQuery(id+"F2.wireOp",EDGE,"E30"),sQuery(id+"F2.wireOp",EDGE,"E31"),sQuery(id+"F2.wireOp",EDGE,"E32"),sQuery(id+"F2.wireOp",EDGE,"E33"),sQuery(id+"F2.wireOp",EDGE,"E34")])],"isStart":false}),makeQuery(id+"F7.opExtrude","CAP_FACE",FACE,{"disambiguationData":[OSD([sQuery(id+"F6.wireOp",EDGE,"E45.0"),sQuery(id+"F6.wireOp",EDGE,"E48"),sQuery(id+"F6.wireOp",EDGE,"E50"),sQuery(id+"F6.wireOp",EDGE,"E51")])],"isStart":true}),makeQuery(id+"F7.opExtrude","CAP_FACE",FACE,{"disambiguationData":[OSD([sQuery(id+"F6.wireOp",EDGE,"E53.MirrorCS"),sQuery(id+"F6.wireOp",EDGE,"E54.MirrorCS"),sQuery(id+"F6.wireOp",EDGE,"E55.MirrorCS"),sQuery(id+"F6.wireOp",EDGE,"E56.MirrorCS")])],"isStart":true})]}),makeQuery(id+"F9.opExtrude","CAP_FACE",FACE,{"disambiguationData":[OSD([sQuery(id+"F8.wireOp",EDGE,"E57.0"),sQuery(id+"F8.wireOp",EDGE,"E58"),sQuery(id+"F8.wireOp",EDGE,"E59"),sQuery(id+"F8.wireOp",EDGE,"E60")])],"isStart":true}),makeQuery(id+"F9.opExtrude","CAP_FACE",FACE,{"disambiguationData":[OSD([sQuery(id+"F8.wireOp",EDGE,"E67.MirrorCS"),sQuery(id+"F8.wireOp",EDGE,"E68.MirrorCS"),sQuery(id+"F8.wireOp",EDGE,"E69.MirrorCS"),sQuery(id+"F8.wireOp",EDGE,"E70.MirrorCS")])],"isStart":true})]}),makeQuery(id+"F11.opExtrude","CAP_FACE",FACE,{"disambiguationData":[OSD([sQuery(id+"F10.wireOp",EDGE,"E72.0"),sQuery(id+"F10.wireOp",EDGE,"E74"),sQuery(id+"F10.wireOp",EDGE,"E76"),sQuery(id+"F10.wireOp",EDGE,"E77"),sQuery(id+"F10.wireOp",EDGE,"E80")])],"isStart":false}),makeQuery(id+"F11.opExtrude","CAP_FACE",FACE,{"disambiguationData":[OSD([sQuery(id+"F10.wireOp",EDGE,"E82.MirrorCS"),sQuery(id+"F10.wireOp",EDGE,"E83.MirrorCS"),sQuery(id+"F10.wireOp",EDGE,"E84.MirrorCS"),sQuery(id+"F10.wireOp",EDGE,"E85.MirrorCS"),sQuery(id+"F10.wireOp",EDGE,"E86.MirrorCS")])],"isStart":false})]}),makeQuery(id+"F20.opExtrude","CAP_FACE",FACE,{"disambiguationData":[OSD([sQuery(id+"F19.wireOp",EDGE,"E119.0"),sQuery(id+"F19.wireOp",EDGE,"E120.0"),sQuery(id+"F19.wireOp",EDGE,"E121.0"),sQuery(id+"F19.wireOp",EDGE,"E122")])],"isStart":true})]}),makeQuery(id+"F24.opExtrude","CAP_FACE",FACE,{"disambiguationData":[OSD([sQuery(id+"F23.wireOp",EDGE,"E129"),sQuery(id+"F23.wireOp",EDGE,"E133"),sQuery(id+"F23.wireOp",EDGE,"E134"),sQuery(id+"F23.wireOp",EDGE,"E135"),sQuery(id+"F23.wireOp",EDGE,"E136"),sQuery(id+"F23.wireOp",EDGE,"E137"),sQuery(id+"F23.wireOp",EDGE,"E138")])],"isStart":true})]});
            var sketch = newSketch(context, id + "F30", { "sketchPlane" : qUnion([Q0])});
            skCircle(sketch, "E193.0", {"center": v(-3.87, -15.14) * mm, "radius": 1.5 * mm, "construction": true});
            skCircle(sketch, "E194", {"center": v(-3.87, -15.14) * mm, "radius": 2.8 * mm});
            skSolve(sketch);
        }
        {
            var Q0;
            Q0 = qSketchRegion(id + "F30", true);
            extrude(context, id + "F31", {"entities" : qUnion([Q0]), "operationType" : NewBodyOperationType.REMOVE, "oppositeDirection" : true, "depth" : 2 * mm});
        }
        {
            var Q0;
            Q0=makeQuery(id+"F24.boolean.opBoolean","MERGE",FACE,{"derivedFrom":[makeQuery(id+"F20.boolean.opBoolean","MERGE",FACE,{"derivedFrom":[makeQuery(id+"F11.boolean.opBoolean","MERGE",FACE,{"derivedFrom":[makeQuery(id+"F9.boolean.opBoolean","MERGE",FACE,{"derivedFrom":[makeQuery(id+"F7.boolean.opBoolean","MERGE",FACE,{"derivedFrom":[makeQuery(id+"F4.opExtrude","CAP_FACE",FACE,{"disambiguationData":[OSD([sQuery(id+"F2.wireOp",EDGE,"E19.0"),sQuery(id+"F2.wireOp",EDGE,"E20.0"),sQuery(id+"F2.wireOp",EDGE,"E21.0"),sQuery(id+"F2.wireOp",EDGE,"E22.0"),sQuery(id+"F2.wireOp",EDGE,"E23.0"),sQuery(id+"F2.wireOp",EDGE,"E24.0"),sQuery(id+"F2.wireOp",EDGE,"E25.0"),sQuery(id+"F2.wireOp",EDGE,"E26.0"),sQuery(id+"F2.wireOp",EDGE,"E27.0"),sQuery(id+"F2.wireOp",EDGE,"E28.0"),sQuery(id+"F2.wireOp",EDGE,"E29"),sQuery(id+"F2.wireOp",EDGE,"E30"),sQuery(id+"F2.wireOp",EDGE,"E31"),sQuery(id+"F2.wireOp",EDGE,"E32"),sQuery(id+"F2.wireOp",EDGE,"E33"),sQuery(id+"F2.wireOp",EDGE,"E34")])],"isStart":false}),makeQuery(id+"F7.opExtrude","CAP_FACE",FACE,{"disambiguationData":[OSD([sQuery(id+"F6.wireOp",EDGE,"E45.0"),sQuery(id+"F6.wireOp",EDGE,"E48"),sQuery(id+"F6.wireOp",EDGE,"E50"),sQuery(id+"F6.wireOp",EDGE,"E51")])],"isStart":true}),makeQuery(id+"F7.opExtrude","CAP_FACE",FACE,{"disambiguationData":[OSD([sQuery(id+"F6.wireOp",EDGE,"E53.MirrorCS"),sQuery(id+"F6.wireOp",EDGE,"E54.MirrorCS"),sQuery(id+"F6.wireOp",EDGE,"E55.MirrorCS"),sQuery(id+"F6.wireOp",EDGE,"E56.MirrorCS")])],"isStart":true})]}),makeQuery(id+"F9.opExtrude","CAP_FACE",FACE,{"disambiguationData":[OSD([sQuery(id+"F8.wireOp",EDGE,"E57.0"),sQuery(id+"F8.wireOp",EDGE,"E58"),sQuery(id+"F8.wireOp",EDGE,"E59"),sQuery(id+"F8.wireOp",EDGE,"E60")])],"isStart":true}),makeQuery(id+"F9.opExtrude","CAP_FACE",FACE,{"disambiguationData":[OSD([sQuery(id+"F8.wireOp",EDGE,"E67.MirrorCS"),sQuery(id+"F8.wireOp",EDGE,"E68.MirrorCS"),sQuery(id+"F8.wireOp",EDGE,"E69.MirrorCS"),sQuery(id+"F8.wireOp",EDGE,"E70.MirrorCS")])],"isStart":true})]}),makeQuery(id+"F11.opExtrude","CAP_FACE",FACE,{"disambiguationData":[OSD([sQuery(id+"F10.wireOp",EDGE,"E72.0"),sQuery(id+"F10.wireOp",EDGE,"E74"),sQuery(id+"F10.wireOp",EDGE,"E76"),sQuery(id+"F10.wireOp",EDGE,"E77"),sQuery(id+"F10.wireOp",EDGE,"E80")])],"isStart":false}),makeQuery(id+"F11.opExtrude","CAP_FACE",FACE,{"disambiguationData":[OSD([sQuery(id+"F10.wireOp",EDGE,"E82.MirrorCS"),sQuery(id+"F10.wireOp",EDGE,"E83.MirrorCS"),sQuery(id+"F10.wireOp",EDGE,"E84.MirrorCS"),sQuery(id+"F10.wireOp",EDGE,"E85.MirrorCS"),sQuery(id+"F10.wireOp",EDGE,"E86.MirrorCS")])],"isStart":false})]}),makeQuery(id+"F20.opExtrude","CAP_FACE",FACE,{"disambiguationData":[OSD([sQuery(id+"F19.wireOp",EDGE,"E119.0"),sQuery(id+"F19.wireOp",EDGE,"E120.0"),sQuery(id+"F19.wireOp",EDGE,"E121.0"),sQuery(id+"F19.wireOp",EDGE,"E122")])],"isStart":true})]}),makeQuery(id+"F24.opExtrude","CAP_FACE",FACE,{"disambiguationData":[OSD([sQuery(id+"F23.wireOp",EDGE,"E129"),sQuery(id+"F23.wireOp",EDGE,"E133"),sQuery(id+"F23.wireOp",EDGE,"E134"),sQuery(id+"F23.wireOp",EDGE,"E135"),sQuery(id+"F23.wireOp",EDGE,"E136"),sQuery(id+"F23.wireOp",EDGE,"E137"),sQuery(id+"F23.wireOp",EDGE,"E138")])],"isStart":true})]});
            var sketch = newSketch(context, id + "F32", { "sketchPlane" : qUnion([Q0])});
            skArc(sketch, "E195.0", {"start": v(91.36, -9.36) * mm, "mid": v(99.21, 0) * mm, "end": v(91.36, 9.36) * mm, "construction": true});
            skLineSegment(sketch, "E196", {"start": v(89.71, 0) * mm, "end": v(130.71, 0) * mm, "construction": true});
            skArc(sketch, "E197", {"start": v(134.71, -4) * mm, "mid": v(138.71, 0) * mm, "end": v(134.71, 4) * mm});
            skLineSegment(sketch, "E198", {"start": v(130.52, 4) * mm, "end": v(134.71, 4) * mm});
            skLineSegment(sketch, "E199", {"start": v(130.52, -4) * mm, "end": v(134.71, -4) * mm});
            skArc(sketch, "E200.0", {"start": v(130.52, -4) * mm, "mid": v(130.71, 0) * mm, "end": v(130.52, 4) * mm});
            skPoint(sketch, "E201.orphan", {"position": v(94.43, -40.73) * mm});
            skPoint(sketch, "E202.orphan", {"position": v(96.83, 40.38) * mm});
            skCircle(sketch, "E203", {"center": v(134.71, 0) * mm, "radius": 1.55 * mm});
            skArc(sketch, "E204.0", {"start": v(94.43, -40.73) * mm, "mid": v(130.7, -1.21) * mm, "end": v(96.83, 40.38) * mm, "construction": true});
            skCircle(sketch, "E205", {"center": v(89.71, 0) * mm, "radius": 41 * mm, "construction": true});
            skSolve(sketch);
        }
        {
            var Q0;
            Q0 = qSketchRegion(id + "F32", true);
            var Q1;
            {var subQ0=sQuery(id+"F2.wireOp",EDGE,"E33");var subQ1=sQuery(id+"F2.wireOp",EDGE,"E32");var subQ2=sQuery(id+"F2.wireOp",EDGE,"E31");var subQ3=makeQuery(id+"F1.opExtrude","SWEPT_FACE",FACE,{"disambiguationData":[OSD([sQuery(id+"F0.wireOp",EDGE,"E13")])]});var subQ5=sQuery(id+"F2.wireOp",EDGE,"E28.0");var subQ7=sQuery(id+"F6.wireOp",EDGE,"E48");var subQ8=sQuery(id+"F6.wireOp",EDGE,"E50");var subQ10=sQuery(id+"F6.wireOp",EDGE,"E51");var subQ13=sQuery(id+"F10.wireOp",EDGE,"E77");var subQ14=sQuery(id+"F10.wireOp",EDGE,"E76");var subQ15=sQuery(id+"F10.wireOp",EDGE,"E74");var subQ16=sQuery(id+"F8.wireOp",EDGE,"E70.MirrorCS");var subQ17=sQuery(id+"F8.wireOp",EDGE,"E68.MirrorCS");var subQ18=sQuery(id+"F8.wireOp",EDGE,"E67.MirrorCS");var subQ19=sQuery(id+"F2.wireOp",EDGE,"E25.0");var subQ22=sQuery(id+"F2.wireOp",EDGE,"E24.0");var subQ24=sQuery(id+"F2.wireOp",EDGE,"E26.0");var subQ26=makeQuery(id+"F1.opExtrude","SWEPT_FACE",FACE,{"disambiguationData":[OSD([sQuery(id+"F0.wireOp",EDGE,"E1")])]});var subQ29=sQuery(id+"F2.wireOp",EDGE,"E27.0");var subQ31=sQuery(id+"F2.wireOp",EDGE,"E34");var subQ32=sQuery(id+"F2.wireOp",EDGE,"E30");var subQ33=sQuery(id+"F2.wireOp",EDGE,"E29");var subQ35=makeQuery(id+"F11.boolean.opBoolean","MERGE",FACE,{"derivedFrom":[makeQuery(id+"F9.boolean.opBoolean","MERGE",FACE,{"derivedFrom":[makeQuery(id+"F7.boolean.opBoolean","MERGE",FACE,{"derivedFrom":[makeQuery(id+"F3.boolean.opBoolean","SPLIT",FACE,{"disambiguationData":[TD([subQ26])],"derivedFrom":makeQuery(id+"F3.opExtrude","CAP_FACE",FACE,{"disambiguationData":[OSD([sQuery(id+"F2.wireOp",EDGE,"E19.0"),sQuery(id+"F2.wireOp",EDGE,"E20.0"),sQuery(id+"F2.wireOp",EDGE,"E21.0"),sQuery(id+"F2.wireOp",EDGE,"E22.0"),sQuery(id+"F2.wireOp",EDGE,"E23.0"),subQ22,subQ19,subQ24,subQ29,subQ5,subQ33,subQ32,subQ2,subQ1,subQ0,subQ31])],"isStart":true})}),makeQuery(id+"F7.opExtrude","CAP_FACE",FACE,{"disambiguationData":[OSD([sQuery(id+"F6.wireOp",EDGE,"E45.0"),subQ7,subQ8,subQ10])],"isStart":false})]}),makeQuery(id+"F9.opExtrude","CAP_FACE",FACE,{"disambiguationData":[OSD([subQ18,subQ17,sQuery(id+"F8.wireOp",EDGE,"E69.MirrorCS"),subQ16])],"isStart":false})]}),makeQuery(id+"F11.opExtrude","CAP_FACE",FACE,{"disambiguationData":[OSD([sQuery(id+"F10.wireOp",EDGE,"E72.0"),subQ15,subQ14,subQ13,sQuery(id+"F10.wireOp",EDGE,"E80")])],"isStart":true})]});Q1=makeQuery(id+"F22.boolean.opBoolean","MERGE",FACE,{"derivedFrom":[makeQuery(id+"F17.boolean.opBoolean","SPLIT",FACE,{"disambiguationData":[TD([subQ26])],"derivedFrom":subQ35}),makeQuery(id+"F17.boolean.opBoolean","SPLIT",FACE,{"disambiguationData":[TD([subQ3])],"derivedFrom":subQ35}),makeQuery(id+"F22.opExtrude","CAP_FACE",FACE,{"disambiguationData":[OSD([sQuery(id+"F21.wireOp",EDGE,"E123.0.0"),sQuery(id+"F21.wireOp",EDGE,"E123.0.1"),sQuery(id+"F21.wireOp",EDGE,"E123.0.2"),sQuery(id+"F21.wireOp",EDGE,"E123.0.3"),sQuery(id+"F21.wireOp",EDGE,"E123.0.10"),sQuery(id+"F21.wireOp",EDGE,"E123.0.11"),sQuery(id+"F21.wireOp",EDGE,"E124.0"),sQuery(id+"F21.wireOp",EDGE,"E124.3"),sQuery(id+"F21.wireOp",EDGE,"E124.4"),sQuery(id+"F21.wireOp",EDGE,"E124.6"),sQuery(id+"F21.wireOp",EDGE,"E124.11"),sQuery(id+"F21.wireOp",EDGE,"E125.trimOffspring")])],"isStart":false})]});}
            extrude(context, id + "F33", {"entities" : qUnion([Q0]), "operationType" : NewBodyOperationType.ADD, "endBound" : BoundingType.UP_TO_SURFACE, "oppositeDirection" : true, "endBoundEntityFace" : qUnion([Q1]), "depth" : 25 * mm});
        }
        {
            var Q0;
            Q0=makeQuery(id+"F33.boolean.opBoolean","MERGE",FACE,{"derivedFrom":[makeQuery(id+"F24.boolean.opBoolean","MERGE",FACE,{"derivedFrom":[makeQuery(id+"F20.boolean.opBoolean","MERGE",FACE,{"derivedFrom":[makeQuery(id+"F11.boolean.opBoolean","MERGE",FACE,{"derivedFrom":[makeQuery(id+"F9.boolean.opBoolean","MERGE",FACE,{"derivedFrom":[makeQuery(id+"F7.boolean.opBoolean","MERGE",FACE,{"derivedFrom":[makeQuery(id+"F4.opExtrude","CAP_FACE",FACE,{"disambiguationData":[OSD([sQuery(id+"F2.wireOp",EDGE,"E19.0"),sQuery(id+"F2.wireOp",EDGE,"E20.0"),sQuery(id+"F2.wireOp",EDGE,"E21.0"),sQuery(id+"F2.wireOp",EDGE,"E22.0"),sQuery(id+"F2.wireOp",EDGE,"E23.0"),sQuery(id+"F2.wireOp",EDGE,"E24.0"),sQuery(id+"F2.wireOp",EDGE,"E25.0"),sQuery(id+"F2.wireOp",EDGE,"E26.0"),sQuery(id+"F2.wireOp",EDGE,"E27.0"),sQuery(id+"F2.wireOp",EDGE,"E28.0"),sQuery(id+"F2.wireOp",EDGE,"E29"),sQuery(id+"F2.wireOp",EDGE,"E30"),sQuery(id+"F2.wireOp",EDGE,"E31"),sQuery(id+"F2.wireOp",EDGE,"E32"),sQuery(id+"F2.wireOp",EDGE,"E33"),sQuery(id+"F2.wireOp",EDGE,"E34")])],"isStart":false}),makeQuery(id+"F7.opExtrude","CAP_FACE",FACE,{"disambiguationData":[OSD([sQuery(id+"F6.wireOp",EDGE,"E45.0"),sQuery(id+"F6.wireOp",EDGE,"E48"),sQuery(id+"F6.wireOp",EDGE,"E50"),sQuery(id+"F6.wireOp",EDGE,"E51")])],"isStart":true}),makeQuery(id+"F7.opExtrude","CAP_FACE",FACE,{"disambiguationData":[OSD([sQuery(id+"F6.wireOp",EDGE,"E53.MirrorCS"),sQuery(id+"F6.wireOp",EDGE,"E54.MirrorCS"),sQuery(id+"F6.wireOp",EDGE,"E55.MirrorCS"),sQuery(id+"F6.wireOp",EDGE,"E56.MirrorCS")])],"isStart":true})]}),makeQuery(id+"F9.opExtrude","CAP_FACE",FACE,{"disambiguationData":[OSD([sQuery(id+"F8.wireOp",EDGE,"E57.0"),sQuery(id+"F8.wireOp",EDGE,"E58"),sQuery(id+"F8.wireOp",EDGE,"E59"),sQuery(id+"F8.wireOp",EDGE,"E60")])],"isStart":true}),makeQuery(id+"F9.opExtrude","CAP_FACE",FACE,{"disambiguationData":[OSD([sQuery(id+"F8.wireOp",EDGE,"E67.MirrorCS"),sQuery(id+"F8.wireOp",EDGE,"E68.MirrorCS"),sQuery(id+"F8.wireOp",EDGE,"E69.MirrorCS"),sQuery(id+"F8.wireOp",EDGE,"E70.MirrorCS")])],"isStart":true})]}),makeQuery(id+"F11.opExtrude","CAP_FACE",FACE,{"disambiguationData":[OSD([sQuery(id+"F10.wireOp",EDGE,"E72.0"),sQuery(id+"F10.wireOp",EDGE,"E74"),sQuery(id+"F10.wireOp",EDGE,"E76"),sQuery(id+"F10.wireOp",EDGE,"E77"),sQuery(id+"F10.wireOp",EDGE,"E80")])],"isStart":false}),makeQuery(id+"F11.opExtrude","CAP_FACE",FACE,{"disambiguationData":[OSD([sQuery(id+"F10.wireOp",EDGE,"E82.MirrorCS"),sQuery(id+"F10.wireOp",EDGE,"E83.MirrorCS"),sQuery(id+"F10.wireOp",EDGE,"E84.MirrorCS"),sQuery(id+"F10.wireOp",EDGE,"E85.MirrorCS"),sQuery(id+"F10.wireOp",EDGE,"E86.MirrorCS")])],"isStart":false})]}),makeQuery(id+"F20.opExtrude","CAP_FACE",FACE,{"disambiguationData":[OSD([sQuery(id+"F19.wireOp",EDGE,"E119.0"),sQuery(id+"F19.wireOp",EDGE,"E120.0"),sQuery(id+"F19.wireOp",EDGE,"E121.0"),sQuery(id+"F19.wireOp",EDGE,"E122")])],"isStart":true})]}),makeQuery(id+"F24.opExtrude","CAP_FACE",FACE,{"disambiguationData":[OSD([sQuery(id+"F23.wireOp",EDGE,"E129"),sQuery(id+"F23.wireOp",EDGE,"E133"),sQuery(id+"F23.wireOp",EDGE,"E134"),sQuery(id+"F23.wireOp",EDGE,"E135"),sQuery(id+"F23.wireOp",EDGE,"E136"),sQuery(id+"F23.wireOp",EDGE,"E137"),sQuery(id+"F23.wireOp",EDGE,"E138")])],"isStart":true})]}),makeQuery(id+"F33.opExtrude","CAP_FACE",FACE,{"disambiguationData":[OSD([sQuery(id+"F32.wireOp",EDGE,"E197"),sQuery(id+"F32.wireOp",EDGE,"E198"),sQuery(id+"F32.wireOp",EDGE,"E199"),sQuery(id+"F32.wireOp",EDGE,"E200.0"),sQuery(id+"F32.wireOp",EDGE,"E203")])],"isStart":true})]});
            var sketch = newSketch(context, id + "F34", { "sketchPlane" : qUnion([Q0])});
            skCircle(sketch, "E206.0", {"center": v(134.71, 0) * mm, "radius": 1.55 * mm, "construction": true});
            skCircle(sketch, "E207", {"center": v(134.71, 0) * mm, "radius": 2.8 * mm});
            skSolve(sketch);
        }
        {
            var Q0;
            Q0 = qSketchRegion(id + "F34", true);
            extrude(context, id + "F35", {"entities" : qUnion([Q0]), "operationType" : NewBodyOperationType.REMOVE, "oppositeDirection" : true, "depth" : 2 * mm});
        }
    });
